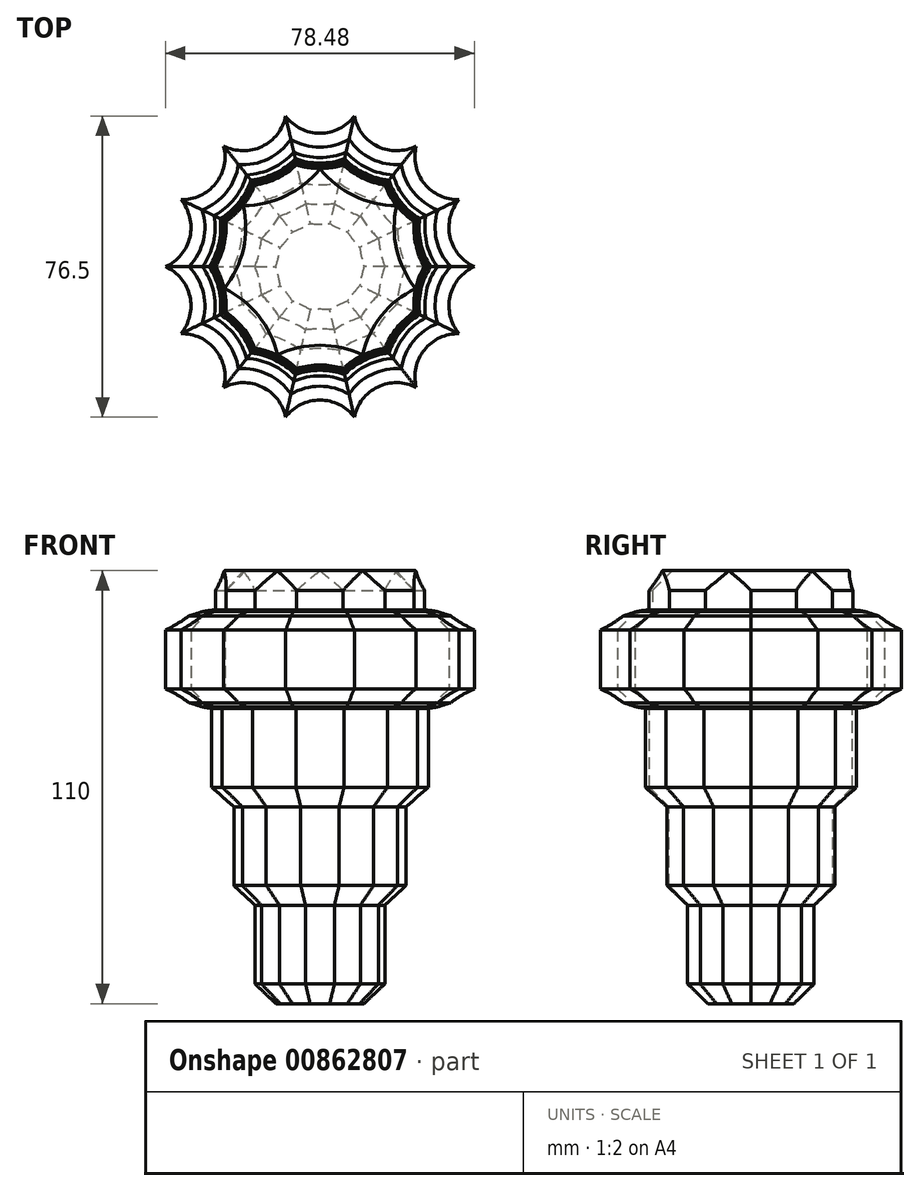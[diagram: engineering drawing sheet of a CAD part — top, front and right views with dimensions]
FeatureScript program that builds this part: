
annotation { "Feature Type Name" : "Feature", "Feature Type Description" : "" }
export const myFeature = defineFeature(function(context is Context, id is Id, definition is map)
    precondition{}
    {
        {
            var Q0;
            Q0=qCreatedBy(makeId("Top.planeOp"),FACE);
            var sketch = newSketch(context, id + "F0", { "sketchPlane" : qUnion([Q0])});
            skCircle(sketch, "E0", {"center": v(0, 44.83) * mm, "radius": 10.93 * mm});
            skCircle(sketch, "E1.1.0", {"center": v(-19.45, 40.39) * mm, "radius": 10.93 * mm});
            skCircle(sketch, "E1.2.0", {"center": v(-35.05, 27.95) * mm, "radius": 10.93 * mm});
            skCircle(sketch, "E1.3.0", {"center": v(-43.7, 9.98) * mm, "radius": 10.93 * mm});
            skCircle(sketch, "E1.4.0", {"center": v(-43.7, -9.98) * mm, "radius": 10.93 * mm});
            skCircle(sketch, "E1.5.0", {"center": v(-35.05, -27.95) * mm, "radius": 10.93 * mm});
            skCircle(sketch, "E1.6.0", {"center": v(-19.45, -40.39) * mm, "radius": 10.93 * mm});
            skCircle(sketch, "E1.7.0", {"center": v(0, -44.83) * mm, "radius": 10.93 * mm});
            skCircle(sketch, "E1.8.0", {"center": v(19.45, -40.39) * mm, "radius": 10.93 * mm});
            skCircle(sketch, "E1.9.0", {"center": v(35.05, -27.95) * mm, "radius": 10.93 * mm});
            skPoint(sketch, "E1.center", {"position": v(0, 0) * mm});
            skCircle(sketch, "E2.1.10.0", {"center": v(43.7, -9.98) * mm, "radius": 10.93 * mm});
            skCircle(sketch, "E2.1.11.0", {"center": v(43.7, 9.98) * mm, "radius": 10.93 * mm});
            skCircle(sketch, "E3.1.12.0", {"center": v(35.05, 27.95) * mm, "radius": 10.93 * mm});
            skCircle(sketch, "E3.1.13.0", {"center": v(19.45, 40.39) * mm, "radius": 10.93 * mm});
            skSolve(sketch);
        }
        {
            var Q0;
            {var subQ15=sQuery(id+"F0.wireOp",EDGE,"E1.1.0");var subQ16=sQuery(id+"F0.wireOp",EDGE,"E0");var subQ17=makeQuery(id+"F0.imprint","INTERSECT",VERTEX,{"disambiguationData":[OD(1.0)],"derivedFrom":[subQ16,subQ15]});Q0=makeQuery(id+"F0.imprint","IMPRINT",FACE,{"disambiguationData":[TD([[makeQuery(id+"F0.imprint","IMPRINT",EDGE,{"disambiguationData":[TD([[subQ17,-1.0]])],"derivedFrom":subQ16}),-1.0]])]});}
            extrude(context, id + "F1", {"entities" : qUnion([Q0]), "depth" : 25 * mm, "offsetDistance" : 25 * mm});
        }
        {
            var Q0;
            Q0=makeQuery(id+"F1.opExtrude","CAP_EDGE",EDGE,{"disambiguationData":[OSD([sQuery(id+"F0.wireOp",EDGE,"E1.2.0")])],"isStart":false});
            var Q1;
            Q1=makeQuery(id+"F1.opExtrude","CAP_EDGE",EDGE,{"disambiguationData":[OSD([sQuery(id+"F0.wireOp",EDGE,"E1.1.0")])],"isStart":false});
            var Q2;
            Q2=makeQuery(id+"F1.opExtrude","CAP_EDGE",EDGE,{"disambiguationData":[OSD([sQuery(id+"F0.wireOp",EDGE,"E0")])],"isStart":false});
            var Q3;
            Q3=makeQuery(id+"F1.opExtrude","CAP_EDGE",EDGE,{"disambiguationData":[OSD([sQuery(id+"F0.wireOp",EDGE,"E3.1.13.0")])],"isStart":false});
            var Q4;
            Q4=makeQuery(id+"F1.opExtrude","CAP_EDGE",EDGE,{"disambiguationData":[OSD([sQuery(id+"F0.wireOp",EDGE,"E3.1.12.0")])],"isStart":false});
            var Q5;
            Q5=makeQuery(id+"F1.opExtrude","CAP_EDGE",EDGE,{"disambiguationData":[OSD([sQuery(id+"F0.wireOp",EDGE,"E2.1.11.0")])],"isStart":false});
            var Q6;
            Q6=makeQuery(id+"F1.opExtrude","CAP_EDGE",EDGE,{"disambiguationData":[OSD([sQuery(id+"F0.wireOp",EDGE,"E2.1.10.0")])],"isStart":false});
            var Q7;
            Q7=makeQuery(id+"F1.opExtrude","CAP_EDGE",EDGE,{"disambiguationData":[OSD([sQuery(id+"F0.wireOp",EDGE,"E1.9.0")])],"isStart":false});
            var Q8;
            Q8=makeQuery(id+"F1.opExtrude","CAP_EDGE",EDGE,{"disambiguationData":[OSD([sQuery(id+"F0.wireOp",EDGE,"E1.8.0")])],"isStart":false});
            var Q9;
            Q9=makeQuery(id+"F1.opExtrude","CAP_EDGE",EDGE,{"disambiguationData":[OSD([sQuery(id+"F0.wireOp",EDGE,"E1.7.0")])],"isStart":false});
            var Q10;
            Q10=makeQuery(id+"F1.opExtrude","CAP_EDGE",EDGE,{"disambiguationData":[OSD([sQuery(id+"F0.wireOp",EDGE,"E1.6.0")])],"isStart":false});
            var Q11;
            Q11=makeQuery(id+"F1.opExtrude","CAP_EDGE",EDGE,{"disambiguationData":[OSD([sQuery(id+"F0.wireOp",EDGE,"E1.5.0")])],"isStart":false});
            var Q12;
            Q12=makeQuery(id+"F1.opExtrude","CAP_EDGE",EDGE,{"disambiguationData":[OSD([sQuery(id+"F0.wireOp",EDGE,"E1.4.0")])],"isStart":false});
            var Q13;
            Q13=makeQuery(id+"F1.opExtrude","CAP_EDGE",EDGE,{"disambiguationData":[OSD([sQuery(id+"F0.wireOp",EDGE,"E1.3.0")])],"isStart":false});
            chamfer(context, id + "F2", {"entities" : qUnion([Q0, Q1, Q2, Q3, Q4, Q5, Q6, Q7, Q8, Q9, Q10, Q11, Q12, Q13]), "width" : 5 * mm, "tangentPropagation" : true});
        }
        {
            var Q0;
            {var subQ0=sQuery(id+"F0.wireOp",EDGE,"E1.2.0");Q0=makeQuery(id+"F2.opChamfer","BLEND_EDGE",EDGE,{"blendedFrom":[makeQuery(id+"F1.opExtrude","CAP_EDGE",EDGE,{"disambiguationData":[OSD([subQ0])],"isStart":false}),makeQuery(id+"F1.opExtrude","CAP_FACE",FACE,{"disambiguationData":[OSD([sQuery(id+"F0.wireOp",EDGE,"E0"),sQuery(id+"F0.wireOp",EDGE,"E1.1.0"),subQ0,sQuery(id+"F0.wireOp",EDGE,"E1.3.0"),sQuery(id+"F0.wireOp",EDGE,"E1.4.0"),sQuery(id+"F0.wireOp",EDGE,"E1.5.0"),sQuery(id+"F0.wireOp",EDGE,"E1.6.0"),sQuery(id+"F0.wireOp",EDGE,"E1.7.0"),sQuery(id+"F0.wireOp",EDGE,"E1.8.0"),sQuery(id+"F0.wireOp",EDGE,"E1.9.0"),sQuery(id+"F0.wireOp",EDGE,"E2.1.10.0"),sQuery(id+"F0.wireOp",EDGE,"E2.1.11.0"),sQuery(id+"F0.wireOp",EDGE,"E3.1.12.0"),sQuery(id+"F0.wireOp",EDGE,"E3.1.13.0")])],"isStart":false})],"blendedInto":[makeQuery(id+"F1.opExtrude","CAP_FACE",FACE,{"disambiguationData":[OSD([sQuery(id+"F0.wireOp",EDGE,"E0"),sQuery(id+"F0.wireOp",EDGE,"E1.1.0"),subQ0,sQuery(id+"F0.wireOp",EDGE,"E1.3.0"),sQuery(id+"F0.wireOp",EDGE,"E1.4.0"),sQuery(id+"F0.wireOp",EDGE,"E1.5.0"),sQuery(id+"F0.wireOp",EDGE,"E1.6.0"),sQuery(id+"F0.wireOp",EDGE,"E1.7.0"),sQuery(id+"F0.wireOp",EDGE,"E1.8.0"),sQuery(id+"F0.wireOp",EDGE,"E1.9.0"),sQuery(id+"F0.wireOp",EDGE,"E2.1.10.0"),sQuery(id+"F0.wireOp",EDGE,"E2.1.11.0"),sQuery(id+"F0.wireOp",EDGE,"E3.1.12.0"),sQuery(id+"F0.wireOp",EDGE,"E3.1.13.0")])],"isStart":false})]});}
            var Q1;
            {var subQ0=sQuery(id+"F0.wireOp",EDGE,"E1.1.0");Q1=makeQuery(id+"F2.opChamfer","BLEND_EDGE",EDGE,{"blendedFrom":[makeQuery(id+"F1.opExtrude","CAP_EDGE",EDGE,{"disambiguationData":[OSD([subQ0])],"isStart":false}),makeQuery(id+"F1.opExtrude","CAP_FACE",FACE,{"disambiguationData":[OSD([sQuery(id+"F0.wireOp",EDGE,"E0"),subQ0,sQuery(id+"F0.wireOp",EDGE,"E1.2.0"),sQuery(id+"F0.wireOp",EDGE,"E1.3.0"),sQuery(id+"F0.wireOp",EDGE,"E1.4.0"),sQuery(id+"F0.wireOp",EDGE,"E1.5.0"),sQuery(id+"F0.wireOp",EDGE,"E1.6.0"),sQuery(id+"F0.wireOp",EDGE,"E1.7.0"),sQuery(id+"F0.wireOp",EDGE,"E1.8.0"),sQuery(id+"F0.wireOp",EDGE,"E1.9.0"),sQuery(id+"F0.wireOp",EDGE,"E2.1.10.0"),sQuery(id+"F0.wireOp",EDGE,"E2.1.11.0"),sQuery(id+"F0.wireOp",EDGE,"E3.1.12.0"),sQuery(id+"F0.wireOp",EDGE,"E3.1.13.0")])],"isStart":false})],"blendedInto":[makeQuery(id+"F1.opExtrude","CAP_FACE",FACE,{"disambiguationData":[OSD([sQuery(id+"F0.wireOp",EDGE,"E0"),subQ0,sQuery(id+"F0.wireOp",EDGE,"E1.2.0"),sQuery(id+"F0.wireOp",EDGE,"E1.3.0"),sQuery(id+"F0.wireOp",EDGE,"E1.4.0"),sQuery(id+"F0.wireOp",EDGE,"E1.5.0"),sQuery(id+"F0.wireOp",EDGE,"E1.6.0"),sQuery(id+"F0.wireOp",EDGE,"E1.7.0"),sQuery(id+"F0.wireOp",EDGE,"E1.8.0"),sQuery(id+"F0.wireOp",EDGE,"E1.9.0"),sQuery(id+"F0.wireOp",EDGE,"E2.1.10.0"),sQuery(id+"F0.wireOp",EDGE,"E2.1.11.0"),sQuery(id+"F0.wireOp",EDGE,"E3.1.12.0"),sQuery(id+"F0.wireOp",EDGE,"E3.1.13.0")])],"isStart":false})]});}
            var Q2;
            {var subQ0=sQuery(id+"F0.wireOp",EDGE,"E0");Q2=makeQuery(id+"F2.opChamfer","BLEND_EDGE",EDGE,{"blendedFrom":[makeQuery(id+"F1.opExtrude","CAP_EDGE",EDGE,{"disambiguationData":[OSD([subQ0])],"isStart":false}),makeQuery(id+"F1.opExtrude","CAP_FACE",FACE,{"disambiguationData":[OSD([subQ0,sQuery(id+"F0.wireOp",EDGE,"E1.1.0"),sQuery(id+"F0.wireOp",EDGE,"E1.2.0"),sQuery(id+"F0.wireOp",EDGE,"E1.3.0"),sQuery(id+"F0.wireOp",EDGE,"E1.4.0"),sQuery(id+"F0.wireOp",EDGE,"E1.5.0"),sQuery(id+"F0.wireOp",EDGE,"E1.6.0"),sQuery(id+"F0.wireOp",EDGE,"E1.7.0"),sQuery(id+"F0.wireOp",EDGE,"E1.8.0"),sQuery(id+"F0.wireOp",EDGE,"E1.9.0"),sQuery(id+"F0.wireOp",EDGE,"E2.1.10.0"),sQuery(id+"F0.wireOp",EDGE,"E2.1.11.0"),sQuery(id+"F0.wireOp",EDGE,"E3.1.12.0"),sQuery(id+"F0.wireOp",EDGE,"E3.1.13.0")])],"isStart":false})],"blendedInto":[makeQuery(id+"F1.opExtrude","CAP_FACE",FACE,{"disambiguationData":[OSD([subQ0,sQuery(id+"F0.wireOp",EDGE,"E1.1.0"),sQuery(id+"F0.wireOp",EDGE,"E1.2.0"),sQuery(id+"F0.wireOp",EDGE,"E1.3.0"),sQuery(id+"F0.wireOp",EDGE,"E1.4.0"),sQuery(id+"F0.wireOp",EDGE,"E1.5.0"),sQuery(id+"F0.wireOp",EDGE,"E1.6.0"),sQuery(id+"F0.wireOp",EDGE,"E1.7.0"),sQuery(id+"F0.wireOp",EDGE,"E1.8.0"),sQuery(id+"F0.wireOp",EDGE,"E1.9.0"),sQuery(id+"F0.wireOp",EDGE,"E2.1.10.0"),sQuery(id+"F0.wireOp",EDGE,"E2.1.11.0"),sQuery(id+"F0.wireOp",EDGE,"E3.1.12.0"),sQuery(id+"F0.wireOp",EDGE,"E3.1.13.0")])],"isStart":false})]});}
            var Q3;
            {var subQ0=sQuery(id+"F0.wireOp",EDGE,"E3.1.13.0");Q3=makeQuery(id+"F2.opChamfer","BLEND_EDGE",EDGE,{"blendedFrom":[makeQuery(id+"F1.opExtrude","CAP_EDGE",EDGE,{"disambiguationData":[OSD([subQ0])],"isStart":false}),makeQuery(id+"F1.opExtrude","CAP_FACE",FACE,{"disambiguationData":[OSD([sQuery(id+"F0.wireOp",EDGE,"E0"),sQuery(id+"F0.wireOp",EDGE,"E1.1.0"),sQuery(id+"F0.wireOp",EDGE,"E1.2.0"),sQuery(id+"F0.wireOp",EDGE,"E1.3.0"),sQuery(id+"F0.wireOp",EDGE,"E1.4.0"),sQuery(id+"F0.wireOp",EDGE,"E1.5.0"),sQuery(id+"F0.wireOp",EDGE,"E1.6.0"),sQuery(id+"F0.wireOp",EDGE,"E1.7.0"),sQuery(id+"F0.wireOp",EDGE,"E1.8.0"),sQuery(id+"F0.wireOp",EDGE,"E1.9.0"),sQuery(id+"F0.wireOp",EDGE,"E2.1.10.0"),sQuery(id+"F0.wireOp",EDGE,"E2.1.11.0"),sQuery(id+"F0.wireOp",EDGE,"E3.1.12.0"),subQ0])],"isStart":false})],"blendedInto":[makeQuery(id+"F1.opExtrude","CAP_FACE",FACE,{"disambiguationData":[OSD([sQuery(id+"F0.wireOp",EDGE,"E0"),sQuery(id+"F0.wireOp",EDGE,"E1.1.0"),sQuery(id+"F0.wireOp",EDGE,"E1.2.0"),sQuery(id+"F0.wireOp",EDGE,"E1.3.0"),sQuery(id+"F0.wireOp",EDGE,"E1.4.0"),sQuery(id+"F0.wireOp",EDGE,"E1.5.0"),sQuery(id+"F0.wireOp",EDGE,"E1.6.0"),sQuery(id+"F0.wireOp",EDGE,"E1.7.0"),sQuery(id+"F0.wireOp",EDGE,"E1.8.0"),sQuery(id+"F0.wireOp",EDGE,"E1.9.0"),sQuery(id+"F0.wireOp",EDGE,"E2.1.10.0"),sQuery(id+"F0.wireOp",EDGE,"E2.1.11.0"),sQuery(id+"F0.wireOp",EDGE,"E3.1.12.0"),subQ0])],"isStart":false})]});}
            var Q4;
            {var subQ0=sQuery(id+"F0.wireOp",EDGE,"E3.1.12.0");Q4=makeQuery(id+"F2.opChamfer","BLEND_EDGE",EDGE,{"blendedFrom":[makeQuery(id+"F1.opExtrude","CAP_EDGE",EDGE,{"disambiguationData":[OSD([subQ0])],"isStart":false}),makeQuery(id+"F1.opExtrude","CAP_FACE",FACE,{"disambiguationData":[OSD([sQuery(id+"F0.wireOp",EDGE,"E0"),sQuery(id+"F0.wireOp",EDGE,"E1.1.0"),sQuery(id+"F0.wireOp",EDGE,"E1.2.0"),sQuery(id+"F0.wireOp",EDGE,"E1.3.0"),sQuery(id+"F0.wireOp",EDGE,"E1.4.0"),sQuery(id+"F0.wireOp",EDGE,"E1.5.0"),sQuery(id+"F0.wireOp",EDGE,"E1.6.0"),sQuery(id+"F0.wireOp",EDGE,"E1.7.0"),sQuery(id+"F0.wireOp",EDGE,"E1.8.0"),sQuery(id+"F0.wireOp",EDGE,"E1.9.0"),sQuery(id+"F0.wireOp",EDGE,"E2.1.10.0"),sQuery(id+"F0.wireOp",EDGE,"E2.1.11.0"),subQ0,sQuery(id+"F0.wireOp",EDGE,"E3.1.13.0")])],"isStart":false})],"blendedInto":[makeQuery(id+"F1.opExtrude","CAP_FACE",FACE,{"disambiguationData":[OSD([sQuery(id+"F0.wireOp",EDGE,"E0"),sQuery(id+"F0.wireOp",EDGE,"E1.1.0"),sQuery(id+"F0.wireOp",EDGE,"E1.2.0"),sQuery(id+"F0.wireOp",EDGE,"E1.3.0"),sQuery(id+"F0.wireOp",EDGE,"E1.4.0"),sQuery(id+"F0.wireOp",EDGE,"E1.5.0"),sQuery(id+"F0.wireOp",EDGE,"E1.6.0"),sQuery(id+"F0.wireOp",EDGE,"E1.7.0"),sQuery(id+"F0.wireOp",EDGE,"E1.8.0"),sQuery(id+"F0.wireOp",EDGE,"E1.9.0"),sQuery(id+"F0.wireOp",EDGE,"E2.1.10.0"),sQuery(id+"F0.wireOp",EDGE,"E2.1.11.0"),subQ0,sQuery(id+"F0.wireOp",EDGE,"E3.1.13.0")])],"isStart":false})]});}
            var Q5;
            {var subQ0=sQuery(id+"F0.wireOp",EDGE,"E2.1.11.0");Q5=makeQuery(id+"F2.opChamfer","BLEND_EDGE",EDGE,{"blendedFrom":[makeQuery(id+"F1.opExtrude","CAP_EDGE",EDGE,{"disambiguationData":[OSD([subQ0])],"isStart":false}),makeQuery(id+"F1.opExtrude","CAP_FACE",FACE,{"disambiguationData":[OSD([sQuery(id+"F0.wireOp",EDGE,"E0"),sQuery(id+"F0.wireOp",EDGE,"E1.1.0"),sQuery(id+"F0.wireOp",EDGE,"E1.2.0"),sQuery(id+"F0.wireOp",EDGE,"E1.3.0"),sQuery(id+"F0.wireOp",EDGE,"E1.4.0"),sQuery(id+"F0.wireOp",EDGE,"E1.5.0"),sQuery(id+"F0.wireOp",EDGE,"E1.6.0"),sQuery(id+"F0.wireOp",EDGE,"E1.7.0"),sQuery(id+"F0.wireOp",EDGE,"E1.8.0"),sQuery(id+"F0.wireOp",EDGE,"E1.9.0"),sQuery(id+"F0.wireOp",EDGE,"E2.1.10.0"),subQ0,sQuery(id+"F0.wireOp",EDGE,"E3.1.12.0"),sQuery(id+"F0.wireOp",EDGE,"E3.1.13.0")])],"isStart":false})],"blendedInto":[makeQuery(id+"F1.opExtrude","CAP_FACE",FACE,{"disambiguationData":[OSD([sQuery(id+"F0.wireOp",EDGE,"E0"),sQuery(id+"F0.wireOp",EDGE,"E1.1.0"),sQuery(id+"F0.wireOp",EDGE,"E1.2.0"),sQuery(id+"F0.wireOp",EDGE,"E1.3.0"),sQuery(id+"F0.wireOp",EDGE,"E1.4.0"),sQuery(id+"F0.wireOp",EDGE,"E1.5.0"),sQuery(id+"F0.wireOp",EDGE,"E1.6.0"),sQuery(id+"F0.wireOp",EDGE,"E1.7.0"),sQuery(id+"F0.wireOp",EDGE,"E1.8.0"),sQuery(id+"F0.wireOp",EDGE,"E1.9.0"),sQuery(id+"F0.wireOp",EDGE,"E2.1.10.0"),subQ0,sQuery(id+"F0.wireOp",EDGE,"E3.1.12.0"),sQuery(id+"F0.wireOp",EDGE,"E3.1.13.0")])],"isStart":false})]});}
            var Q6;
            {var subQ0=sQuery(id+"F0.wireOp",EDGE,"E2.1.10.0");Q6=makeQuery(id+"F2.opChamfer","BLEND_EDGE",EDGE,{"blendedFrom":[makeQuery(id+"F1.opExtrude","CAP_EDGE",EDGE,{"disambiguationData":[OSD([subQ0])],"isStart":false}),makeQuery(id+"F1.opExtrude","CAP_FACE",FACE,{"disambiguationData":[OSD([sQuery(id+"F0.wireOp",EDGE,"E0"),sQuery(id+"F0.wireOp",EDGE,"E1.1.0"),sQuery(id+"F0.wireOp",EDGE,"E1.2.0"),sQuery(id+"F0.wireOp",EDGE,"E1.3.0"),sQuery(id+"F0.wireOp",EDGE,"E1.4.0"),sQuery(id+"F0.wireOp",EDGE,"E1.5.0"),sQuery(id+"F0.wireOp",EDGE,"E1.6.0"),sQuery(id+"F0.wireOp",EDGE,"E1.7.0"),sQuery(id+"F0.wireOp",EDGE,"E1.8.0"),sQuery(id+"F0.wireOp",EDGE,"E1.9.0"),subQ0,sQuery(id+"F0.wireOp",EDGE,"E2.1.11.0"),sQuery(id+"F0.wireOp",EDGE,"E3.1.12.0"),sQuery(id+"F0.wireOp",EDGE,"E3.1.13.0")])],"isStart":false})],"blendedInto":[makeQuery(id+"F1.opExtrude","CAP_FACE",FACE,{"disambiguationData":[OSD([sQuery(id+"F0.wireOp",EDGE,"E0"),sQuery(id+"F0.wireOp",EDGE,"E1.1.0"),sQuery(id+"F0.wireOp",EDGE,"E1.2.0"),sQuery(id+"F0.wireOp",EDGE,"E1.3.0"),sQuery(id+"F0.wireOp",EDGE,"E1.4.0"),sQuery(id+"F0.wireOp",EDGE,"E1.5.0"),sQuery(id+"F0.wireOp",EDGE,"E1.6.0"),sQuery(id+"F0.wireOp",EDGE,"E1.7.0"),sQuery(id+"F0.wireOp",EDGE,"E1.8.0"),sQuery(id+"F0.wireOp",EDGE,"E1.9.0"),subQ0,sQuery(id+"F0.wireOp",EDGE,"E2.1.11.0"),sQuery(id+"F0.wireOp",EDGE,"E3.1.12.0"),sQuery(id+"F0.wireOp",EDGE,"E3.1.13.0")])],"isStart":false})]});}
            var Q7;
            {var subQ0=sQuery(id+"F0.wireOp",EDGE,"E1.9.0");Q7=makeQuery(id+"F2.opChamfer","BLEND_EDGE",EDGE,{"blendedFrom":[makeQuery(id+"F1.opExtrude","CAP_EDGE",EDGE,{"disambiguationData":[OSD([subQ0])],"isStart":false}),makeQuery(id+"F1.opExtrude","CAP_FACE",FACE,{"disambiguationData":[OSD([sQuery(id+"F0.wireOp",EDGE,"E0"),sQuery(id+"F0.wireOp",EDGE,"E1.1.0"),sQuery(id+"F0.wireOp",EDGE,"E1.2.0"),sQuery(id+"F0.wireOp",EDGE,"E1.3.0"),sQuery(id+"F0.wireOp",EDGE,"E1.4.0"),sQuery(id+"F0.wireOp",EDGE,"E1.5.0"),sQuery(id+"F0.wireOp",EDGE,"E1.6.0"),sQuery(id+"F0.wireOp",EDGE,"E1.7.0"),sQuery(id+"F0.wireOp",EDGE,"E1.8.0"),subQ0,sQuery(id+"F0.wireOp",EDGE,"E2.1.10.0"),sQuery(id+"F0.wireOp",EDGE,"E2.1.11.0"),sQuery(id+"F0.wireOp",EDGE,"E3.1.12.0"),sQuery(id+"F0.wireOp",EDGE,"E3.1.13.0")])],"isStart":false})],"blendedInto":[makeQuery(id+"F1.opExtrude","CAP_FACE",FACE,{"disambiguationData":[OSD([sQuery(id+"F0.wireOp",EDGE,"E0"),sQuery(id+"F0.wireOp",EDGE,"E1.1.0"),sQuery(id+"F0.wireOp",EDGE,"E1.2.0"),sQuery(id+"F0.wireOp",EDGE,"E1.3.0"),sQuery(id+"F0.wireOp",EDGE,"E1.4.0"),sQuery(id+"F0.wireOp",EDGE,"E1.5.0"),sQuery(id+"F0.wireOp",EDGE,"E1.6.0"),sQuery(id+"F0.wireOp",EDGE,"E1.7.0"),sQuery(id+"F0.wireOp",EDGE,"E1.8.0"),subQ0,sQuery(id+"F0.wireOp",EDGE,"E2.1.10.0"),sQuery(id+"F0.wireOp",EDGE,"E2.1.11.0"),sQuery(id+"F0.wireOp",EDGE,"E3.1.12.0"),sQuery(id+"F0.wireOp",EDGE,"E3.1.13.0")])],"isStart":false})]});}
            var Q8;
            {var subQ0=sQuery(id+"F0.wireOp",EDGE,"E1.8.0");Q8=makeQuery(id+"F2.opChamfer","BLEND_EDGE",EDGE,{"blendedFrom":[makeQuery(id+"F1.opExtrude","CAP_EDGE",EDGE,{"disambiguationData":[OSD([subQ0])],"isStart":false}),makeQuery(id+"F1.opExtrude","CAP_FACE",FACE,{"disambiguationData":[OSD([sQuery(id+"F0.wireOp",EDGE,"E0"),sQuery(id+"F0.wireOp",EDGE,"E1.1.0"),sQuery(id+"F0.wireOp",EDGE,"E1.2.0"),sQuery(id+"F0.wireOp",EDGE,"E1.3.0"),sQuery(id+"F0.wireOp",EDGE,"E1.4.0"),sQuery(id+"F0.wireOp",EDGE,"E1.5.0"),sQuery(id+"F0.wireOp",EDGE,"E1.6.0"),sQuery(id+"F0.wireOp",EDGE,"E1.7.0"),subQ0,sQuery(id+"F0.wireOp",EDGE,"E1.9.0"),sQuery(id+"F0.wireOp",EDGE,"E2.1.10.0"),sQuery(id+"F0.wireOp",EDGE,"E2.1.11.0"),sQuery(id+"F0.wireOp",EDGE,"E3.1.12.0"),sQuery(id+"F0.wireOp",EDGE,"E3.1.13.0")])],"isStart":false})],"blendedInto":[makeQuery(id+"F1.opExtrude","CAP_FACE",FACE,{"disambiguationData":[OSD([sQuery(id+"F0.wireOp",EDGE,"E0"),sQuery(id+"F0.wireOp",EDGE,"E1.1.0"),sQuery(id+"F0.wireOp",EDGE,"E1.2.0"),sQuery(id+"F0.wireOp",EDGE,"E1.3.0"),sQuery(id+"F0.wireOp",EDGE,"E1.4.0"),sQuery(id+"F0.wireOp",EDGE,"E1.5.0"),sQuery(id+"F0.wireOp",EDGE,"E1.6.0"),sQuery(id+"F0.wireOp",EDGE,"E1.7.0"),subQ0,sQuery(id+"F0.wireOp",EDGE,"E1.9.0"),sQuery(id+"F0.wireOp",EDGE,"E2.1.10.0"),sQuery(id+"F0.wireOp",EDGE,"E2.1.11.0"),sQuery(id+"F0.wireOp",EDGE,"E3.1.12.0"),sQuery(id+"F0.wireOp",EDGE,"E3.1.13.0")])],"isStart":false})]});}
            var Q9;
            {var subQ0=sQuery(id+"F0.wireOp",EDGE,"E1.7.0");Q9=makeQuery(id+"F2.opChamfer","BLEND_EDGE",EDGE,{"blendedFrom":[makeQuery(id+"F1.opExtrude","CAP_EDGE",EDGE,{"disambiguationData":[OSD([subQ0])],"isStart":false}),makeQuery(id+"F1.opExtrude","CAP_FACE",FACE,{"disambiguationData":[OSD([sQuery(id+"F0.wireOp",EDGE,"E0"),sQuery(id+"F0.wireOp",EDGE,"E1.1.0"),sQuery(id+"F0.wireOp",EDGE,"E1.2.0"),sQuery(id+"F0.wireOp",EDGE,"E1.3.0"),sQuery(id+"F0.wireOp",EDGE,"E1.4.0"),sQuery(id+"F0.wireOp",EDGE,"E1.5.0"),sQuery(id+"F0.wireOp",EDGE,"E1.6.0"),subQ0,sQuery(id+"F0.wireOp",EDGE,"E1.8.0"),sQuery(id+"F0.wireOp",EDGE,"E1.9.0"),sQuery(id+"F0.wireOp",EDGE,"E2.1.10.0"),sQuery(id+"F0.wireOp",EDGE,"E2.1.11.0"),sQuery(id+"F0.wireOp",EDGE,"E3.1.12.0"),sQuery(id+"F0.wireOp",EDGE,"E3.1.13.0")])],"isStart":false})],"blendedInto":[makeQuery(id+"F1.opExtrude","CAP_FACE",FACE,{"disambiguationData":[OSD([sQuery(id+"F0.wireOp",EDGE,"E0"),sQuery(id+"F0.wireOp",EDGE,"E1.1.0"),sQuery(id+"F0.wireOp",EDGE,"E1.2.0"),sQuery(id+"F0.wireOp",EDGE,"E1.3.0"),sQuery(id+"F0.wireOp",EDGE,"E1.4.0"),sQuery(id+"F0.wireOp",EDGE,"E1.5.0"),sQuery(id+"F0.wireOp",EDGE,"E1.6.0"),subQ0,sQuery(id+"F0.wireOp",EDGE,"E1.8.0"),sQuery(id+"F0.wireOp",EDGE,"E1.9.0"),sQuery(id+"F0.wireOp",EDGE,"E2.1.10.0"),sQuery(id+"F0.wireOp",EDGE,"E2.1.11.0"),sQuery(id+"F0.wireOp",EDGE,"E3.1.12.0"),sQuery(id+"F0.wireOp",EDGE,"E3.1.13.0")])],"isStart":false})]});}
            var Q10;
            {var subQ0=sQuery(id+"F0.wireOp",EDGE,"E1.6.0");Q10=makeQuery(id+"F2.opChamfer","BLEND_EDGE",EDGE,{"blendedFrom":[makeQuery(id+"F1.opExtrude","CAP_EDGE",EDGE,{"disambiguationData":[OSD([subQ0])],"isStart":false}),makeQuery(id+"F1.opExtrude","CAP_FACE",FACE,{"disambiguationData":[OSD([sQuery(id+"F0.wireOp",EDGE,"E0"),sQuery(id+"F0.wireOp",EDGE,"E1.1.0"),sQuery(id+"F0.wireOp",EDGE,"E1.2.0"),sQuery(id+"F0.wireOp",EDGE,"E1.3.0"),sQuery(id+"F0.wireOp",EDGE,"E1.4.0"),sQuery(id+"F0.wireOp",EDGE,"E1.5.0"),subQ0,sQuery(id+"F0.wireOp",EDGE,"E1.7.0"),sQuery(id+"F0.wireOp",EDGE,"E1.8.0"),sQuery(id+"F0.wireOp",EDGE,"E1.9.0"),sQuery(id+"F0.wireOp",EDGE,"E2.1.10.0"),sQuery(id+"F0.wireOp",EDGE,"E2.1.11.0"),sQuery(id+"F0.wireOp",EDGE,"E3.1.12.0"),sQuery(id+"F0.wireOp",EDGE,"E3.1.13.0")])],"isStart":false})],"blendedInto":[makeQuery(id+"F1.opExtrude","CAP_FACE",FACE,{"disambiguationData":[OSD([sQuery(id+"F0.wireOp",EDGE,"E0"),sQuery(id+"F0.wireOp",EDGE,"E1.1.0"),sQuery(id+"F0.wireOp",EDGE,"E1.2.0"),sQuery(id+"F0.wireOp",EDGE,"E1.3.0"),sQuery(id+"F0.wireOp",EDGE,"E1.4.0"),sQuery(id+"F0.wireOp",EDGE,"E1.5.0"),subQ0,sQuery(id+"F0.wireOp",EDGE,"E1.7.0"),sQuery(id+"F0.wireOp",EDGE,"E1.8.0"),sQuery(id+"F0.wireOp",EDGE,"E1.9.0"),sQuery(id+"F0.wireOp",EDGE,"E2.1.10.0"),sQuery(id+"F0.wireOp",EDGE,"E2.1.11.0"),sQuery(id+"F0.wireOp",EDGE,"E3.1.12.0"),sQuery(id+"F0.wireOp",EDGE,"E3.1.13.0")])],"isStart":false})]});}
            var Q11;
            {var subQ0=sQuery(id+"F0.wireOp",EDGE,"E1.5.0");Q11=makeQuery(id+"F2.opChamfer","BLEND_EDGE",EDGE,{"blendedFrom":[makeQuery(id+"F1.opExtrude","CAP_EDGE",EDGE,{"disambiguationData":[OSD([subQ0])],"isStart":false}),makeQuery(id+"F1.opExtrude","CAP_FACE",FACE,{"disambiguationData":[OSD([sQuery(id+"F0.wireOp",EDGE,"E0"),sQuery(id+"F0.wireOp",EDGE,"E1.1.0"),sQuery(id+"F0.wireOp",EDGE,"E1.2.0"),sQuery(id+"F0.wireOp",EDGE,"E1.3.0"),sQuery(id+"F0.wireOp",EDGE,"E1.4.0"),subQ0,sQuery(id+"F0.wireOp",EDGE,"E1.6.0"),sQuery(id+"F0.wireOp",EDGE,"E1.7.0"),sQuery(id+"F0.wireOp",EDGE,"E1.8.0"),sQuery(id+"F0.wireOp",EDGE,"E1.9.0"),sQuery(id+"F0.wireOp",EDGE,"E2.1.10.0"),sQuery(id+"F0.wireOp",EDGE,"E2.1.11.0"),sQuery(id+"F0.wireOp",EDGE,"E3.1.12.0"),sQuery(id+"F0.wireOp",EDGE,"E3.1.13.0")])],"isStart":false})],"blendedInto":[makeQuery(id+"F1.opExtrude","CAP_FACE",FACE,{"disambiguationData":[OSD([sQuery(id+"F0.wireOp",EDGE,"E0"),sQuery(id+"F0.wireOp",EDGE,"E1.1.0"),sQuery(id+"F0.wireOp",EDGE,"E1.2.0"),sQuery(id+"F0.wireOp",EDGE,"E1.3.0"),sQuery(id+"F0.wireOp",EDGE,"E1.4.0"),subQ0,sQuery(id+"F0.wireOp",EDGE,"E1.6.0"),sQuery(id+"F0.wireOp",EDGE,"E1.7.0"),sQuery(id+"F0.wireOp",EDGE,"E1.8.0"),sQuery(id+"F0.wireOp",EDGE,"E1.9.0"),sQuery(id+"F0.wireOp",EDGE,"E2.1.10.0"),sQuery(id+"F0.wireOp",EDGE,"E2.1.11.0"),sQuery(id+"F0.wireOp",EDGE,"E3.1.12.0"),sQuery(id+"F0.wireOp",EDGE,"E3.1.13.0")])],"isStart":false})]});}
            var Q12;
            {var subQ0=sQuery(id+"F0.wireOp",EDGE,"E1.4.0");Q12=makeQuery(id+"F2.opChamfer","BLEND_EDGE",EDGE,{"blendedFrom":[makeQuery(id+"F1.opExtrude","CAP_EDGE",EDGE,{"disambiguationData":[OSD([subQ0])],"isStart":false}),makeQuery(id+"F1.opExtrude","CAP_FACE",FACE,{"disambiguationData":[OSD([sQuery(id+"F0.wireOp",EDGE,"E0"),sQuery(id+"F0.wireOp",EDGE,"E1.1.0"),sQuery(id+"F0.wireOp",EDGE,"E1.2.0"),sQuery(id+"F0.wireOp",EDGE,"E1.3.0"),subQ0,sQuery(id+"F0.wireOp",EDGE,"E1.5.0"),sQuery(id+"F0.wireOp",EDGE,"E1.6.0"),sQuery(id+"F0.wireOp",EDGE,"E1.7.0"),sQuery(id+"F0.wireOp",EDGE,"E1.8.0"),sQuery(id+"F0.wireOp",EDGE,"E1.9.0"),sQuery(id+"F0.wireOp",EDGE,"E2.1.10.0"),sQuery(id+"F0.wireOp",EDGE,"E2.1.11.0"),sQuery(id+"F0.wireOp",EDGE,"E3.1.12.0"),sQuery(id+"F0.wireOp",EDGE,"E3.1.13.0")])],"isStart":false})],"blendedInto":[makeQuery(id+"F1.opExtrude","CAP_FACE",FACE,{"disambiguationData":[OSD([sQuery(id+"F0.wireOp",EDGE,"E0"),sQuery(id+"F0.wireOp",EDGE,"E1.1.0"),sQuery(id+"F0.wireOp",EDGE,"E1.2.0"),sQuery(id+"F0.wireOp",EDGE,"E1.3.0"),subQ0,sQuery(id+"F0.wireOp",EDGE,"E1.5.0"),sQuery(id+"F0.wireOp",EDGE,"E1.6.0"),sQuery(id+"F0.wireOp",EDGE,"E1.7.0"),sQuery(id+"F0.wireOp",EDGE,"E1.8.0"),sQuery(id+"F0.wireOp",EDGE,"E1.9.0"),sQuery(id+"F0.wireOp",EDGE,"E2.1.10.0"),sQuery(id+"F0.wireOp",EDGE,"E2.1.11.0"),sQuery(id+"F0.wireOp",EDGE,"E3.1.12.0"),sQuery(id+"F0.wireOp",EDGE,"E3.1.13.0")])],"isStart":false})]});}
            var Q13;
            {var subQ0=sQuery(id+"F0.wireOp",EDGE,"E1.3.0");Q13=makeQuery(id+"F2.opChamfer","BLEND_EDGE",EDGE,{"blendedFrom":[makeQuery(id+"F1.opExtrude","CAP_EDGE",EDGE,{"disambiguationData":[OSD([subQ0])],"isStart":false}),makeQuery(id+"F1.opExtrude","CAP_FACE",FACE,{"disambiguationData":[OSD([sQuery(id+"F0.wireOp",EDGE,"E0"),sQuery(id+"F0.wireOp",EDGE,"E1.1.0"),sQuery(id+"F0.wireOp",EDGE,"E1.2.0"),subQ0,sQuery(id+"F0.wireOp",EDGE,"E1.4.0"),sQuery(id+"F0.wireOp",EDGE,"E1.5.0"),sQuery(id+"F0.wireOp",EDGE,"E1.6.0"),sQuery(id+"F0.wireOp",EDGE,"E1.7.0"),sQuery(id+"F0.wireOp",EDGE,"E1.8.0"),sQuery(id+"F0.wireOp",EDGE,"E1.9.0"),sQuery(id+"F0.wireOp",EDGE,"E2.1.10.0"),sQuery(id+"F0.wireOp",EDGE,"E2.1.11.0"),sQuery(id+"F0.wireOp",EDGE,"E3.1.12.0"),sQuery(id+"F0.wireOp",EDGE,"E3.1.13.0")])],"isStart":false})],"blendedInto":[makeQuery(id+"F1.opExtrude","CAP_FACE",FACE,{"disambiguationData":[OSD([sQuery(id+"F0.wireOp",EDGE,"E0"),sQuery(id+"F0.wireOp",EDGE,"E1.1.0"),sQuery(id+"F0.wireOp",EDGE,"E1.2.0"),subQ0,sQuery(id+"F0.wireOp",EDGE,"E1.4.0"),sQuery(id+"F0.wireOp",EDGE,"E1.5.0"),sQuery(id+"F0.wireOp",EDGE,"E1.6.0"),sQuery(id+"F0.wireOp",EDGE,"E1.7.0"),sQuery(id+"F0.wireOp",EDGE,"E1.8.0"),sQuery(id+"F0.wireOp",EDGE,"E1.9.0"),sQuery(id+"F0.wireOp",EDGE,"E2.1.10.0"),sQuery(id+"F0.wireOp",EDGE,"E2.1.11.0"),sQuery(id+"F0.wireOp",EDGE,"E3.1.12.0"),sQuery(id+"F0.wireOp",EDGE,"E3.1.13.0")])],"isStart":false})]});}
            chamfer(context, id + "F3", {"entities" : qUnion([Q0, Q1, Q2, Q3, Q4, Q5, Q6, Q7, Q8, Q9, Q10, Q11, Q12, Q13]), "width" : 5 * mm, "tangentPropagation" : true});
        }
        {
            var Q0;
            {var subQ0=sQuery(id+"F0.wireOp",EDGE,"E1.2.0");var subQ1=makeQuery(id+"F1.opExtrude","CAP_FACE",FACE,{"disambiguationData":[OSD([sQuery(id+"F0.wireOp",EDGE,"E0"),sQuery(id+"F0.wireOp",EDGE,"E1.1.0"),subQ0,sQuery(id+"F0.wireOp",EDGE,"E1.3.0"),sQuery(id+"F0.wireOp",EDGE,"E1.4.0"),sQuery(id+"F0.wireOp",EDGE,"E1.5.0"),sQuery(id+"F0.wireOp",EDGE,"E1.6.0"),sQuery(id+"F0.wireOp",EDGE,"E1.7.0"),sQuery(id+"F0.wireOp",EDGE,"E1.8.0"),sQuery(id+"F0.wireOp",EDGE,"E1.9.0"),sQuery(id+"F0.wireOp",EDGE,"E2.1.10.0"),sQuery(id+"F0.wireOp",EDGE,"E2.1.11.0"),sQuery(id+"F0.wireOp",EDGE,"E3.1.12.0"),sQuery(id+"F0.wireOp",EDGE,"E3.1.13.0")])],"isStart":false});Q0=makeQuery(id+"F3.opChamfer","BLEND_EDGE",EDGE,{"blendedFrom":[makeQuery(id+"F2.opChamfer","BLEND_EDGE",EDGE,{"blendedFrom":[makeQuery(id+"F1.opExtrude","CAP_EDGE",EDGE,{"disambiguationData":[OSD([subQ0])],"isStart":false}),subQ1],"blendedInto":[subQ1]}),subQ1],"blendedInto":[subQ1]});}
            var Q1;
            {var subQ0=sQuery(id+"F0.wireOp",EDGE,"E1.1.0");var subQ1=makeQuery(id+"F1.opExtrude","CAP_FACE",FACE,{"disambiguationData":[OSD([sQuery(id+"F0.wireOp",EDGE,"E0"),subQ0,sQuery(id+"F0.wireOp",EDGE,"E1.2.0"),sQuery(id+"F0.wireOp",EDGE,"E1.3.0"),sQuery(id+"F0.wireOp",EDGE,"E1.4.0"),sQuery(id+"F0.wireOp",EDGE,"E1.5.0"),sQuery(id+"F0.wireOp",EDGE,"E1.6.0"),sQuery(id+"F0.wireOp",EDGE,"E1.7.0"),sQuery(id+"F0.wireOp",EDGE,"E1.8.0"),sQuery(id+"F0.wireOp",EDGE,"E1.9.0"),sQuery(id+"F0.wireOp",EDGE,"E2.1.10.0"),sQuery(id+"F0.wireOp",EDGE,"E2.1.11.0"),sQuery(id+"F0.wireOp",EDGE,"E3.1.12.0"),sQuery(id+"F0.wireOp",EDGE,"E3.1.13.0")])],"isStart":false});Q1=makeQuery(id+"F3.opChamfer","BLEND_EDGE",EDGE,{"blendedFrom":[makeQuery(id+"F2.opChamfer","BLEND_EDGE",EDGE,{"blendedFrom":[makeQuery(id+"F1.opExtrude","CAP_EDGE",EDGE,{"disambiguationData":[OSD([subQ0])],"isStart":false}),subQ1],"blendedInto":[subQ1]}),subQ1],"blendedInto":[subQ1]});}
            var Q2;
            {var subQ0=sQuery(id+"F0.wireOp",EDGE,"E0");var subQ1=makeQuery(id+"F1.opExtrude","CAP_FACE",FACE,{"disambiguationData":[OSD([subQ0,sQuery(id+"F0.wireOp",EDGE,"E1.1.0"),sQuery(id+"F0.wireOp",EDGE,"E1.2.0"),sQuery(id+"F0.wireOp",EDGE,"E1.3.0"),sQuery(id+"F0.wireOp",EDGE,"E1.4.0"),sQuery(id+"F0.wireOp",EDGE,"E1.5.0"),sQuery(id+"F0.wireOp",EDGE,"E1.6.0"),sQuery(id+"F0.wireOp",EDGE,"E1.7.0"),sQuery(id+"F0.wireOp",EDGE,"E1.8.0"),sQuery(id+"F0.wireOp",EDGE,"E1.9.0"),sQuery(id+"F0.wireOp",EDGE,"E2.1.10.0"),sQuery(id+"F0.wireOp",EDGE,"E2.1.11.0"),sQuery(id+"F0.wireOp",EDGE,"E3.1.12.0"),sQuery(id+"F0.wireOp",EDGE,"E3.1.13.0")])],"isStart":false});Q2=makeQuery(id+"F3.opChamfer","BLEND_EDGE",EDGE,{"blendedFrom":[makeQuery(id+"F2.opChamfer","BLEND_EDGE",EDGE,{"blendedFrom":[makeQuery(id+"F1.opExtrude","CAP_EDGE",EDGE,{"disambiguationData":[OSD([subQ0])],"isStart":false}),subQ1],"blendedInto":[subQ1]}),subQ1],"blendedInto":[subQ1]});}
            var Q3;
            {var subQ0=sQuery(id+"F0.wireOp",EDGE,"E3.1.13.0");var subQ1=makeQuery(id+"F1.opExtrude","CAP_FACE",FACE,{"disambiguationData":[OSD([sQuery(id+"F0.wireOp",EDGE,"E0"),sQuery(id+"F0.wireOp",EDGE,"E1.1.0"),sQuery(id+"F0.wireOp",EDGE,"E1.2.0"),sQuery(id+"F0.wireOp",EDGE,"E1.3.0"),sQuery(id+"F0.wireOp",EDGE,"E1.4.0"),sQuery(id+"F0.wireOp",EDGE,"E1.5.0"),sQuery(id+"F0.wireOp",EDGE,"E1.6.0"),sQuery(id+"F0.wireOp",EDGE,"E1.7.0"),sQuery(id+"F0.wireOp",EDGE,"E1.8.0"),sQuery(id+"F0.wireOp",EDGE,"E1.9.0"),sQuery(id+"F0.wireOp",EDGE,"E2.1.10.0"),sQuery(id+"F0.wireOp",EDGE,"E2.1.11.0"),sQuery(id+"F0.wireOp",EDGE,"E3.1.12.0"),subQ0])],"isStart":false});Q3=makeQuery(id+"F3.opChamfer","BLEND_EDGE",EDGE,{"blendedFrom":[makeQuery(id+"F2.opChamfer","BLEND_EDGE",EDGE,{"blendedFrom":[makeQuery(id+"F1.opExtrude","CAP_EDGE",EDGE,{"disambiguationData":[OSD([subQ0])],"isStart":false}),subQ1],"blendedInto":[subQ1]}),subQ1],"blendedInto":[subQ1]});}
            var Q4;
            {var subQ0=sQuery(id+"F0.wireOp",EDGE,"E3.1.12.0");var subQ1=makeQuery(id+"F1.opExtrude","CAP_FACE",FACE,{"disambiguationData":[OSD([sQuery(id+"F0.wireOp",EDGE,"E0"),sQuery(id+"F0.wireOp",EDGE,"E1.1.0"),sQuery(id+"F0.wireOp",EDGE,"E1.2.0"),sQuery(id+"F0.wireOp",EDGE,"E1.3.0"),sQuery(id+"F0.wireOp",EDGE,"E1.4.0"),sQuery(id+"F0.wireOp",EDGE,"E1.5.0"),sQuery(id+"F0.wireOp",EDGE,"E1.6.0"),sQuery(id+"F0.wireOp",EDGE,"E1.7.0"),sQuery(id+"F0.wireOp",EDGE,"E1.8.0"),sQuery(id+"F0.wireOp",EDGE,"E1.9.0"),sQuery(id+"F0.wireOp",EDGE,"E2.1.10.0"),sQuery(id+"F0.wireOp",EDGE,"E2.1.11.0"),subQ0,sQuery(id+"F0.wireOp",EDGE,"E3.1.13.0")])],"isStart":false});Q4=makeQuery(id+"F3.opChamfer","BLEND_EDGE",EDGE,{"blendedFrom":[makeQuery(id+"F2.opChamfer","BLEND_EDGE",EDGE,{"blendedFrom":[makeQuery(id+"F1.opExtrude","CAP_EDGE",EDGE,{"disambiguationData":[OSD([subQ0])],"isStart":false}),subQ1],"blendedInto":[subQ1]}),subQ1],"blendedInto":[subQ1]});}
            var Q5;
            {var subQ0=sQuery(id+"F0.wireOp",EDGE,"E2.1.11.0");var subQ1=makeQuery(id+"F1.opExtrude","CAP_FACE",FACE,{"disambiguationData":[OSD([sQuery(id+"F0.wireOp",EDGE,"E0"),sQuery(id+"F0.wireOp",EDGE,"E1.1.0"),sQuery(id+"F0.wireOp",EDGE,"E1.2.0"),sQuery(id+"F0.wireOp",EDGE,"E1.3.0"),sQuery(id+"F0.wireOp",EDGE,"E1.4.0"),sQuery(id+"F0.wireOp",EDGE,"E1.5.0"),sQuery(id+"F0.wireOp",EDGE,"E1.6.0"),sQuery(id+"F0.wireOp",EDGE,"E1.7.0"),sQuery(id+"F0.wireOp",EDGE,"E1.8.0"),sQuery(id+"F0.wireOp",EDGE,"E1.9.0"),sQuery(id+"F0.wireOp",EDGE,"E2.1.10.0"),subQ0,sQuery(id+"F0.wireOp",EDGE,"E3.1.12.0"),sQuery(id+"F0.wireOp",EDGE,"E3.1.13.0")])],"isStart":false});Q5=makeQuery(id+"F3.opChamfer","BLEND_EDGE",EDGE,{"blendedFrom":[makeQuery(id+"F2.opChamfer","BLEND_EDGE",EDGE,{"blendedFrom":[makeQuery(id+"F1.opExtrude","CAP_EDGE",EDGE,{"disambiguationData":[OSD([subQ0])],"isStart":false}),subQ1],"blendedInto":[subQ1]}),subQ1],"blendedInto":[subQ1]});}
            var Q6;
            {var subQ0=sQuery(id+"F0.wireOp",EDGE,"E2.1.10.0");var subQ1=makeQuery(id+"F1.opExtrude","CAP_FACE",FACE,{"disambiguationData":[OSD([sQuery(id+"F0.wireOp",EDGE,"E0"),sQuery(id+"F0.wireOp",EDGE,"E1.1.0"),sQuery(id+"F0.wireOp",EDGE,"E1.2.0"),sQuery(id+"F0.wireOp",EDGE,"E1.3.0"),sQuery(id+"F0.wireOp",EDGE,"E1.4.0"),sQuery(id+"F0.wireOp",EDGE,"E1.5.0"),sQuery(id+"F0.wireOp",EDGE,"E1.6.0"),sQuery(id+"F0.wireOp",EDGE,"E1.7.0"),sQuery(id+"F0.wireOp",EDGE,"E1.8.0"),sQuery(id+"F0.wireOp",EDGE,"E1.9.0"),subQ0,sQuery(id+"F0.wireOp",EDGE,"E2.1.11.0"),sQuery(id+"F0.wireOp",EDGE,"E3.1.12.0"),sQuery(id+"F0.wireOp",EDGE,"E3.1.13.0")])],"isStart":false});Q6=makeQuery(id+"F3.opChamfer","BLEND_EDGE",EDGE,{"blendedFrom":[makeQuery(id+"F2.opChamfer","BLEND_EDGE",EDGE,{"blendedFrom":[makeQuery(id+"F1.opExtrude","CAP_EDGE",EDGE,{"disambiguationData":[OSD([subQ0])],"isStart":false}),subQ1],"blendedInto":[subQ1]}),subQ1],"blendedInto":[subQ1]});}
            var Q7;
            {var subQ0=sQuery(id+"F0.wireOp",EDGE,"E1.9.0");var subQ1=makeQuery(id+"F1.opExtrude","CAP_FACE",FACE,{"disambiguationData":[OSD([sQuery(id+"F0.wireOp",EDGE,"E0"),sQuery(id+"F0.wireOp",EDGE,"E1.1.0"),sQuery(id+"F0.wireOp",EDGE,"E1.2.0"),sQuery(id+"F0.wireOp",EDGE,"E1.3.0"),sQuery(id+"F0.wireOp",EDGE,"E1.4.0"),sQuery(id+"F0.wireOp",EDGE,"E1.5.0"),sQuery(id+"F0.wireOp",EDGE,"E1.6.0"),sQuery(id+"F0.wireOp",EDGE,"E1.7.0"),sQuery(id+"F0.wireOp",EDGE,"E1.8.0"),subQ0,sQuery(id+"F0.wireOp",EDGE,"E2.1.10.0"),sQuery(id+"F0.wireOp",EDGE,"E2.1.11.0"),sQuery(id+"F0.wireOp",EDGE,"E3.1.12.0"),sQuery(id+"F0.wireOp",EDGE,"E3.1.13.0")])],"isStart":false});Q7=makeQuery(id+"F3.opChamfer","BLEND_EDGE",EDGE,{"blendedFrom":[makeQuery(id+"F2.opChamfer","BLEND_EDGE",EDGE,{"blendedFrom":[makeQuery(id+"F1.opExtrude","CAP_EDGE",EDGE,{"disambiguationData":[OSD([subQ0])],"isStart":false}),subQ1],"blendedInto":[subQ1]}),subQ1],"blendedInto":[subQ1]});}
            var Q8;
            {var subQ0=sQuery(id+"F0.wireOp",EDGE,"E1.8.0");var subQ1=makeQuery(id+"F1.opExtrude","CAP_FACE",FACE,{"disambiguationData":[OSD([sQuery(id+"F0.wireOp",EDGE,"E0"),sQuery(id+"F0.wireOp",EDGE,"E1.1.0"),sQuery(id+"F0.wireOp",EDGE,"E1.2.0"),sQuery(id+"F0.wireOp",EDGE,"E1.3.0"),sQuery(id+"F0.wireOp",EDGE,"E1.4.0"),sQuery(id+"F0.wireOp",EDGE,"E1.5.0"),sQuery(id+"F0.wireOp",EDGE,"E1.6.0"),sQuery(id+"F0.wireOp",EDGE,"E1.7.0"),subQ0,sQuery(id+"F0.wireOp",EDGE,"E1.9.0"),sQuery(id+"F0.wireOp",EDGE,"E2.1.10.0"),sQuery(id+"F0.wireOp",EDGE,"E2.1.11.0"),sQuery(id+"F0.wireOp",EDGE,"E3.1.12.0"),sQuery(id+"F0.wireOp",EDGE,"E3.1.13.0")])],"isStart":false});Q8=makeQuery(id+"F3.opChamfer","BLEND_EDGE",EDGE,{"blendedFrom":[makeQuery(id+"F2.opChamfer","BLEND_EDGE",EDGE,{"blendedFrom":[makeQuery(id+"F1.opExtrude","CAP_EDGE",EDGE,{"disambiguationData":[OSD([subQ0])],"isStart":false}),subQ1],"blendedInto":[subQ1]}),subQ1],"blendedInto":[subQ1]});}
            var Q9;
            {var subQ0=sQuery(id+"F0.wireOp",EDGE,"E1.7.0");var subQ1=makeQuery(id+"F1.opExtrude","CAP_FACE",FACE,{"disambiguationData":[OSD([sQuery(id+"F0.wireOp",EDGE,"E0"),sQuery(id+"F0.wireOp",EDGE,"E1.1.0"),sQuery(id+"F0.wireOp",EDGE,"E1.2.0"),sQuery(id+"F0.wireOp",EDGE,"E1.3.0"),sQuery(id+"F0.wireOp",EDGE,"E1.4.0"),sQuery(id+"F0.wireOp",EDGE,"E1.5.0"),sQuery(id+"F0.wireOp",EDGE,"E1.6.0"),subQ0,sQuery(id+"F0.wireOp",EDGE,"E1.8.0"),sQuery(id+"F0.wireOp",EDGE,"E1.9.0"),sQuery(id+"F0.wireOp",EDGE,"E2.1.10.0"),sQuery(id+"F0.wireOp",EDGE,"E2.1.11.0"),sQuery(id+"F0.wireOp",EDGE,"E3.1.12.0"),sQuery(id+"F0.wireOp",EDGE,"E3.1.13.0")])],"isStart":false});Q9=makeQuery(id+"F3.opChamfer","BLEND_EDGE",EDGE,{"blendedFrom":[makeQuery(id+"F2.opChamfer","BLEND_EDGE",EDGE,{"blendedFrom":[makeQuery(id+"F1.opExtrude","CAP_EDGE",EDGE,{"disambiguationData":[OSD([subQ0])],"isStart":false}),subQ1],"blendedInto":[subQ1]}),subQ1],"blendedInto":[subQ1]});}
            var Q10;
            {var subQ0=sQuery(id+"F0.wireOp",EDGE,"E1.6.0");var subQ1=makeQuery(id+"F1.opExtrude","CAP_FACE",FACE,{"disambiguationData":[OSD([sQuery(id+"F0.wireOp",EDGE,"E0"),sQuery(id+"F0.wireOp",EDGE,"E1.1.0"),sQuery(id+"F0.wireOp",EDGE,"E1.2.0"),sQuery(id+"F0.wireOp",EDGE,"E1.3.0"),sQuery(id+"F0.wireOp",EDGE,"E1.4.0"),sQuery(id+"F0.wireOp",EDGE,"E1.5.0"),subQ0,sQuery(id+"F0.wireOp",EDGE,"E1.7.0"),sQuery(id+"F0.wireOp",EDGE,"E1.8.0"),sQuery(id+"F0.wireOp",EDGE,"E1.9.0"),sQuery(id+"F0.wireOp",EDGE,"E2.1.10.0"),sQuery(id+"F0.wireOp",EDGE,"E2.1.11.0"),sQuery(id+"F0.wireOp",EDGE,"E3.1.12.0"),sQuery(id+"F0.wireOp",EDGE,"E3.1.13.0")])],"isStart":false});Q10=makeQuery(id+"F3.opChamfer","BLEND_EDGE",EDGE,{"blendedFrom":[makeQuery(id+"F2.opChamfer","BLEND_EDGE",EDGE,{"blendedFrom":[makeQuery(id+"F1.opExtrude","CAP_EDGE",EDGE,{"disambiguationData":[OSD([subQ0])],"isStart":false}),subQ1],"blendedInto":[subQ1]}),subQ1],"blendedInto":[subQ1]});}
            var Q11;
            {var subQ0=sQuery(id+"F0.wireOp",EDGE,"E1.5.0");var subQ1=makeQuery(id+"F1.opExtrude","CAP_FACE",FACE,{"disambiguationData":[OSD([sQuery(id+"F0.wireOp",EDGE,"E0"),sQuery(id+"F0.wireOp",EDGE,"E1.1.0"),sQuery(id+"F0.wireOp",EDGE,"E1.2.0"),sQuery(id+"F0.wireOp",EDGE,"E1.3.0"),sQuery(id+"F0.wireOp",EDGE,"E1.4.0"),subQ0,sQuery(id+"F0.wireOp",EDGE,"E1.6.0"),sQuery(id+"F0.wireOp",EDGE,"E1.7.0"),sQuery(id+"F0.wireOp",EDGE,"E1.8.0"),sQuery(id+"F0.wireOp",EDGE,"E1.9.0"),sQuery(id+"F0.wireOp",EDGE,"E2.1.10.0"),sQuery(id+"F0.wireOp",EDGE,"E2.1.11.0"),sQuery(id+"F0.wireOp",EDGE,"E3.1.12.0"),sQuery(id+"F0.wireOp",EDGE,"E3.1.13.0")])],"isStart":false});Q11=makeQuery(id+"F3.opChamfer","BLEND_EDGE",EDGE,{"blendedFrom":[makeQuery(id+"F2.opChamfer","BLEND_EDGE",EDGE,{"blendedFrom":[makeQuery(id+"F1.opExtrude","CAP_EDGE",EDGE,{"disambiguationData":[OSD([subQ0])],"isStart":false}),subQ1],"blendedInto":[subQ1]}),subQ1],"blendedInto":[subQ1]});}
            var Q12;
            {var subQ0=sQuery(id+"F0.wireOp",EDGE,"E1.4.0");var subQ1=makeQuery(id+"F1.opExtrude","CAP_FACE",FACE,{"disambiguationData":[OSD([sQuery(id+"F0.wireOp",EDGE,"E0"),sQuery(id+"F0.wireOp",EDGE,"E1.1.0"),sQuery(id+"F0.wireOp",EDGE,"E1.2.0"),sQuery(id+"F0.wireOp",EDGE,"E1.3.0"),subQ0,sQuery(id+"F0.wireOp",EDGE,"E1.5.0"),sQuery(id+"F0.wireOp",EDGE,"E1.6.0"),sQuery(id+"F0.wireOp",EDGE,"E1.7.0"),sQuery(id+"F0.wireOp",EDGE,"E1.8.0"),sQuery(id+"F0.wireOp",EDGE,"E1.9.0"),sQuery(id+"F0.wireOp",EDGE,"E2.1.10.0"),sQuery(id+"F0.wireOp",EDGE,"E2.1.11.0"),sQuery(id+"F0.wireOp",EDGE,"E3.1.12.0"),sQuery(id+"F0.wireOp",EDGE,"E3.1.13.0")])],"isStart":false});Q12=makeQuery(id+"F3.opChamfer","BLEND_EDGE",EDGE,{"blendedFrom":[makeQuery(id+"F2.opChamfer","BLEND_EDGE",EDGE,{"blendedFrom":[makeQuery(id+"F1.opExtrude","CAP_EDGE",EDGE,{"disambiguationData":[OSD([subQ0])],"isStart":false}),subQ1],"blendedInto":[subQ1]}),subQ1],"blendedInto":[subQ1]});}
            var Q13;
            {var subQ0=sQuery(id+"F0.wireOp",EDGE,"E1.3.0");var subQ1=makeQuery(id+"F1.opExtrude","CAP_FACE",FACE,{"disambiguationData":[OSD([sQuery(id+"F0.wireOp",EDGE,"E0"),sQuery(id+"F0.wireOp",EDGE,"E1.1.0"),sQuery(id+"F0.wireOp",EDGE,"E1.2.0"),subQ0,sQuery(id+"F0.wireOp",EDGE,"E1.4.0"),sQuery(id+"F0.wireOp",EDGE,"E1.5.0"),sQuery(id+"F0.wireOp",EDGE,"E1.6.0"),sQuery(id+"F0.wireOp",EDGE,"E1.7.0"),sQuery(id+"F0.wireOp",EDGE,"E1.8.0"),sQuery(id+"F0.wireOp",EDGE,"E1.9.0"),sQuery(id+"F0.wireOp",EDGE,"E2.1.10.0"),sQuery(id+"F0.wireOp",EDGE,"E2.1.11.0"),sQuery(id+"F0.wireOp",EDGE,"E3.1.12.0"),sQuery(id+"F0.wireOp",EDGE,"E3.1.13.0")])],"isStart":false});Q13=makeQuery(id+"F3.opChamfer","BLEND_EDGE",EDGE,{"blendedFrom":[makeQuery(id+"F2.opChamfer","BLEND_EDGE",EDGE,{"blendedFrom":[makeQuery(id+"F1.opExtrude","CAP_EDGE",EDGE,{"disambiguationData":[OSD([subQ0])],"isStart":false}),subQ1],"blendedInto":[subQ1]}),subQ1],"blendedInto":[subQ1]});}
            chamfer(context, id + "F4", {"entities" : qUnion([Q0, Q1, Q2, Q3, Q4, Q5, Q6, Q7, Q8, Q9, Q10, Q11, Q12, Q13]), "width" : 5 * mm, "tangentPropagation" : true});
        }
        {
            var Q0;
            {var subQ0=sQuery(id+"F0.wireOp",EDGE,"E1.2.0");var subQ1=makeQuery(id+"F1.opExtrude","CAP_FACE",FACE,{"disambiguationData":[OSD([sQuery(id+"F0.wireOp",EDGE,"E0"),sQuery(id+"F0.wireOp",EDGE,"E1.1.0"),subQ0,sQuery(id+"F0.wireOp",EDGE,"E1.3.0"),sQuery(id+"F0.wireOp",EDGE,"E1.4.0"),sQuery(id+"F0.wireOp",EDGE,"E1.5.0"),sQuery(id+"F0.wireOp",EDGE,"E1.6.0"),sQuery(id+"F0.wireOp",EDGE,"E1.7.0"),sQuery(id+"F0.wireOp",EDGE,"E1.8.0"),sQuery(id+"F0.wireOp",EDGE,"E1.9.0"),sQuery(id+"F0.wireOp",EDGE,"E2.1.10.0"),sQuery(id+"F0.wireOp",EDGE,"E2.1.11.0"),sQuery(id+"F0.wireOp",EDGE,"E3.1.12.0"),sQuery(id+"F0.wireOp",EDGE,"E3.1.13.0")])],"isStart":false});var subQ2=subQ1;Q0=makeQuery(id+"F4.opChamfer","BLEND_EDGE",EDGE,{"blendedFrom":[makeQuery(id+"F3.opChamfer","BLEND_EDGE",EDGE,{"blendedFrom":[makeQuery(id+"F2.opChamfer","BLEND_EDGE",EDGE,{"blendedFrom":[makeQuery(id+"F1.opExtrude","CAP_EDGE",EDGE,{"disambiguationData":[OSD([subQ0])],"isStart":false}),subQ1],"blendedInto":[subQ1]}),subQ2],"blendedInto":[subQ2]}),subQ2],"blendedInto":[subQ2]});}
            var Q1;
            {var subQ0=sQuery(id+"F0.wireOp",EDGE,"E1.3.0");var subQ1=makeQuery(id+"F1.opExtrude","CAP_FACE",FACE,{"disambiguationData":[OSD([sQuery(id+"F0.wireOp",EDGE,"E0"),sQuery(id+"F0.wireOp",EDGE,"E1.1.0"),sQuery(id+"F0.wireOp",EDGE,"E1.2.0"),subQ0,sQuery(id+"F0.wireOp",EDGE,"E1.4.0"),sQuery(id+"F0.wireOp",EDGE,"E1.5.0"),sQuery(id+"F0.wireOp",EDGE,"E1.6.0"),sQuery(id+"F0.wireOp",EDGE,"E1.7.0"),sQuery(id+"F0.wireOp",EDGE,"E1.8.0"),sQuery(id+"F0.wireOp",EDGE,"E1.9.0"),sQuery(id+"F0.wireOp",EDGE,"E2.1.10.0"),sQuery(id+"F0.wireOp",EDGE,"E2.1.11.0"),sQuery(id+"F0.wireOp",EDGE,"E3.1.12.0"),sQuery(id+"F0.wireOp",EDGE,"E3.1.13.0")])],"isStart":false});var subQ2=subQ1;Q1=makeQuery(id+"F4.opChamfer","BLEND_EDGE",EDGE,{"blendedFrom":[makeQuery(id+"F3.opChamfer","BLEND_EDGE",EDGE,{"blendedFrom":[makeQuery(id+"F2.opChamfer","BLEND_EDGE",EDGE,{"blendedFrom":[makeQuery(id+"F1.opExtrude","CAP_EDGE",EDGE,{"disambiguationData":[OSD([subQ0])],"isStart":false}),subQ1],"blendedInto":[subQ1]}),subQ2],"blendedInto":[subQ2]}),subQ2],"blendedInto":[subQ2]});}
            var Q2;
            {var subQ0=sQuery(id+"F0.wireOp",EDGE,"E1.4.0");var subQ1=makeQuery(id+"F1.opExtrude","CAP_FACE",FACE,{"disambiguationData":[OSD([sQuery(id+"F0.wireOp",EDGE,"E0"),sQuery(id+"F0.wireOp",EDGE,"E1.1.0"),sQuery(id+"F0.wireOp",EDGE,"E1.2.0"),sQuery(id+"F0.wireOp",EDGE,"E1.3.0"),subQ0,sQuery(id+"F0.wireOp",EDGE,"E1.5.0"),sQuery(id+"F0.wireOp",EDGE,"E1.6.0"),sQuery(id+"F0.wireOp",EDGE,"E1.7.0"),sQuery(id+"F0.wireOp",EDGE,"E1.8.0"),sQuery(id+"F0.wireOp",EDGE,"E1.9.0"),sQuery(id+"F0.wireOp",EDGE,"E2.1.10.0"),sQuery(id+"F0.wireOp",EDGE,"E2.1.11.0"),sQuery(id+"F0.wireOp",EDGE,"E3.1.12.0"),sQuery(id+"F0.wireOp",EDGE,"E3.1.13.0")])],"isStart":false});var subQ2=subQ1;Q2=makeQuery(id+"F4.opChamfer","BLEND_EDGE",EDGE,{"blendedFrom":[makeQuery(id+"F3.opChamfer","BLEND_EDGE",EDGE,{"blendedFrom":[makeQuery(id+"F2.opChamfer","BLEND_EDGE",EDGE,{"blendedFrom":[makeQuery(id+"F1.opExtrude","CAP_EDGE",EDGE,{"disambiguationData":[OSD([subQ0])],"isStart":false}),subQ1],"blendedInto":[subQ1]}),subQ2],"blendedInto":[subQ2]}),subQ2],"blendedInto":[subQ2]});}
            var Q3;
            {var subQ0=sQuery(id+"F0.wireOp",EDGE,"E1.5.0");var subQ1=makeQuery(id+"F1.opExtrude","CAP_FACE",FACE,{"disambiguationData":[OSD([sQuery(id+"F0.wireOp",EDGE,"E0"),sQuery(id+"F0.wireOp",EDGE,"E1.1.0"),sQuery(id+"F0.wireOp",EDGE,"E1.2.0"),sQuery(id+"F0.wireOp",EDGE,"E1.3.0"),sQuery(id+"F0.wireOp",EDGE,"E1.4.0"),subQ0,sQuery(id+"F0.wireOp",EDGE,"E1.6.0"),sQuery(id+"F0.wireOp",EDGE,"E1.7.0"),sQuery(id+"F0.wireOp",EDGE,"E1.8.0"),sQuery(id+"F0.wireOp",EDGE,"E1.9.0"),sQuery(id+"F0.wireOp",EDGE,"E2.1.10.0"),sQuery(id+"F0.wireOp",EDGE,"E2.1.11.0"),sQuery(id+"F0.wireOp",EDGE,"E3.1.12.0"),sQuery(id+"F0.wireOp",EDGE,"E3.1.13.0")])],"isStart":false});var subQ2=subQ1;Q3=makeQuery(id+"F4.opChamfer","BLEND_EDGE",EDGE,{"blendedFrom":[makeQuery(id+"F3.opChamfer","BLEND_EDGE",EDGE,{"blendedFrom":[makeQuery(id+"F2.opChamfer","BLEND_EDGE",EDGE,{"blendedFrom":[makeQuery(id+"F1.opExtrude","CAP_EDGE",EDGE,{"disambiguationData":[OSD([subQ0])],"isStart":false}),subQ1],"blendedInto":[subQ1]}),subQ2],"blendedInto":[subQ2]}),subQ2],"blendedInto":[subQ2]});}
            var Q4;
            {var subQ0=sQuery(id+"F0.wireOp",EDGE,"E1.6.0");var subQ1=makeQuery(id+"F1.opExtrude","CAP_FACE",FACE,{"disambiguationData":[OSD([sQuery(id+"F0.wireOp",EDGE,"E0"),sQuery(id+"F0.wireOp",EDGE,"E1.1.0"),sQuery(id+"F0.wireOp",EDGE,"E1.2.0"),sQuery(id+"F0.wireOp",EDGE,"E1.3.0"),sQuery(id+"F0.wireOp",EDGE,"E1.4.0"),sQuery(id+"F0.wireOp",EDGE,"E1.5.0"),subQ0,sQuery(id+"F0.wireOp",EDGE,"E1.7.0"),sQuery(id+"F0.wireOp",EDGE,"E1.8.0"),sQuery(id+"F0.wireOp",EDGE,"E1.9.0"),sQuery(id+"F0.wireOp",EDGE,"E2.1.10.0"),sQuery(id+"F0.wireOp",EDGE,"E2.1.11.0"),sQuery(id+"F0.wireOp",EDGE,"E3.1.12.0"),sQuery(id+"F0.wireOp",EDGE,"E3.1.13.0")])],"isStart":false});var subQ2=subQ1;Q4=makeQuery(id+"F4.opChamfer","BLEND_EDGE",EDGE,{"blendedFrom":[makeQuery(id+"F3.opChamfer","BLEND_EDGE",EDGE,{"blendedFrom":[makeQuery(id+"F2.opChamfer","BLEND_EDGE",EDGE,{"blendedFrom":[makeQuery(id+"F1.opExtrude","CAP_EDGE",EDGE,{"disambiguationData":[OSD([subQ0])],"isStart":false}),subQ1],"blendedInto":[subQ1]}),subQ2],"blendedInto":[subQ2]}),subQ2],"blendedInto":[subQ2]});}
            var Q5;
            {var subQ0=sQuery(id+"F0.wireOp",EDGE,"E1.7.0");var subQ1=makeQuery(id+"F1.opExtrude","CAP_FACE",FACE,{"disambiguationData":[OSD([sQuery(id+"F0.wireOp",EDGE,"E0"),sQuery(id+"F0.wireOp",EDGE,"E1.1.0"),sQuery(id+"F0.wireOp",EDGE,"E1.2.0"),sQuery(id+"F0.wireOp",EDGE,"E1.3.0"),sQuery(id+"F0.wireOp",EDGE,"E1.4.0"),sQuery(id+"F0.wireOp",EDGE,"E1.5.0"),sQuery(id+"F0.wireOp",EDGE,"E1.6.0"),subQ0,sQuery(id+"F0.wireOp",EDGE,"E1.8.0"),sQuery(id+"F0.wireOp",EDGE,"E1.9.0"),sQuery(id+"F0.wireOp",EDGE,"E2.1.10.0"),sQuery(id+"F0.wireOp",EDGE,"E2.1.11.0"),sQuery(id+"F0.wireOp",EDGE,"E3.1.12.0"),sQuery(id+"F0.wireOp",EDGE,"E3.1.13.0")])],"isStart":false});var subQ2=subQ1;Q5=makeQuery(id+"F4.opChamfer","BLEND_EDGE",EDGE,{"blendedFrom":[makeQuery(id+"F3.opChamfer","BLEND_EDGE",EDGE,{"blendedFrom":[makeQuery(id+"F2.opChamfer","BLEND_EDGE",EDGE,{"blendedFrom":[makeQuery(id+"F1.opExtrude","CAP_EDGE",EDGE,{"disambiguationData":[OSD([subQ0])],"isStart":false}),subQ1],"blendedInto":[subQ1]}),subQ2],"blendedInto":[subQ2]}),subQ2],"blendedInto":[subQ2]});}
            var Q6;
            {var subQ0=sQuery(id+"F0.wireOp",EDGE,"E1.8.0");var subQ1=makeQuery(id+"F1.opExtrude","CAP_FACE",FACE,{"disambiguationData":[OSD([sQuery(id+"F0.wireOp",EDGE,"E0"),sQuery(id+"F0.wireOp",EDGE,"E1.1.0"),sQuery(id+"F0.wireOp",EDGE,"E1.2.0"),sQuery(id+"F0.wireOp",EDGE,"E1.3.0"),sQuery(id+"F0.wireOp",EDGE,"E1.4.0"),sQuery(id+"F0.wireOp",EDGE,"E1.5.0"),sQuery(id+"F0.wireOp",EDGE,"E1.6.0"),sQuery(id+"F0.wireOp",EDGE,"E1.7.0"),subQ0,sQuery(id+"F0.wireOp",EDGE,"E1.9.0"),sQuery(id+"F0.wireOp",EDGE,"E2.1.10.0"),sQuery(id+"F0.wireOp",EDGE,"E2.1.11.0"),sQuery(id+"F0.wireOp",EDGE,"E3.1.12.0"),sQuery(id+"F0.wireOp",EDGE,"E3.1.13.0")])],"isStart":false});var subQ2=subQ1;Q6=makeQuery(id+"F4.opChamfer","BLEND_EDGE",EDGE,{"blendedFrom":[makeQuery(id+"F3.opChamfer","BLEND_EDGE",EDGE,{"blendedFrom":[makeQuery(id+"F2.opChamfer","BLEND_EDGE",EDGE,{"blendedFrom":[makeQuery(id+"F1.opExtrude","CAP_EDGE",EDGE,{"disambiguationData":[OSD([subQ0])],"isStart":false}),subQ1],"blendedInto":[subQ1]}),subQ2],"blendedInto":[subQ2]}),subQ2],"blendedInto":[subQ2]});}
            var Q7;
            {var subQ0=sQuery(id+"F0.wireOp",EDGE,"E1.9.0");var subQ1=makeQuery(id+"F1.opExtrude","CAP_FACE",FACE,{"disambiguationData":[OSD([sQuery(id+"F0.wireOp",EDGE,"E0"),sQuery(id+"F0.wireOp",EDGE,"E1.1.0"),sQuery(id+"F0.wireOp",EDGE,"E1.2.0"),sQuery(id+"F0.wireOp",EDGE,"E1.3.0"),sQuery(id+"F0.wireOp",EDGE,"E1.4.0"),sQuery(id+"F0.wireOp",EDGE,"E1.5.0"),sQuery(id+"F0.wireOp",EDGE,"E1.6.0"),sQuery(id+"F0.wireOp",EDGE,"E1.7.0"),sQuery(id+"F0.wireOp",EDGE,"E1.8.0"),subQ0,sQuery(id+"F0.wireOp",EDGE,"E2.1.10.0"),sQuery(id+"F0.wireOp",EDGE,"E2.1.11.0"),sQuery(id+"F0.wireOp",EDGE,"E3.1.12.0"),sQuery(id+"F0.wireOp",EDGE,"E3.1.13.0")])],"isStart":false});var subQ2=subQ1;Q7=makeQuery(id+"F4.opChamfer","BLEND_EDGE",EDGE,{"blendedFrom":[makeQuery(id+"F3.opChamfer","BLEND_EDGE",EDGE,{"blendedFrom":[makeQuery(id+"F2.opChamfer","BLEND_EDGE",EDGE,{"blendedFrom":[makeQuery(id+"F1.opExtrude","CAP_EDGE",EDGE,{"disambiguationData":[OSD([subQ0])],"isStart":false}),subQ1],"blendedInto":[subQ1]}),subQ2],"blendedInto":[subQ2]}),subQ2],"blendedInto":[subQ2]});}
            var Q8;
            Q8=makeQuery(id+"F1.opExtrude","CAP_FACE",FACE,{"disambiguationData":[OSD([sQuery(id+"F0.wireOp",EDGE,"E0"),sQuery(id+"F0.wireOp",EDGE,"E1.1.0"),sQuery(id+"F0.wireOp",EDGE,"E1.2.0"),sQuery(id+"F0.wireOp",EDGE,"E1.3.0"),sQuery(id+"F0.wireOp",EDGE,"E1.4.0"),sQuery(id+"F0.wireOp",EDGE,"E1.5.0"),sQuery(id+"F0.wireOp",EDGE,"E1.6.0"),sQuery(id+"F0.wireOp",EDGE,"E1.7.0"),sQuery(id+"F0.wireOp",EDGE,"E1.8.0"),sQuery(id+"F0.wireOp",EDGE,"E1.9.0"),sQuery(id+"F0.wireOp",EDGE,"E2.1.10.0"),sQuery(id+"F0.wireOp",EDGE,"E2.1.11.0"),sQuery(id+"F0.wireOp",EDGE,"E3.1.12.0"),sQuery(id+"F0.wireOp",EDGE,"E3.1.13.0")])],"isStart":false});
            chamfer(context, id + "F5", {"entities" : qUnion([Q0, Q1, Q2, Q3, Q4, Q5, Q6, Q7, Q8]), "width" : 5 * mm, "tangentPropagation" : true});
        }
        {
            var Q0;
            Q0=makeQuery(id+"F1.opExtrude","CAP_FACE",FACE,{"disambiguationData":[OSD([sQuery(id+"F0.wireOp",EDGE,"E0"),sQuery(id+"F0.wireOp",EDGE,"E1.1.0"),sQuery(id+"F0.wireOp",EDGE,"E1.2.0"),sQuery(id+"F0.wireOp",EDGE,"E1.3.0"),sQuery(id+"F0.wireOp",EDGE,"E1.4.0"),sQuery(id+"F0.wireOp",EDGE,"E1.5.0"),sQuery(id+"F0.wireOp",EDGE,"E1.6.0"),sQuery(id+"F0.wireOp",EDGE,"E1.7.0"),sQuery(id+"F0.wireOp",EDGE,"E1.8.0"),sQuery(id+"F0.wireOp",EDGE,"E1.9.0"),sQuery(id+"F0.wireOp",EDGE,"E2.1.10.0"),sQuery(id+"F0.wireOp",EDGE,"E2.1.11.0"),sQuery(id+"F0.wireOp",EDGE,"E3.1.12.0"),sQuery(id+"F0.wireOp",EDGE,"E3.1.13.0")])],"isStart":false});
            chamfer(context, id + "F6", {"entities" : qUnion([Q0]), "width" : 5 * mm, "tangentPropagation" : true});
        }
        {
            var Q0;
            Q0=makeQuery(id+"F1.opExtrude","CAP_FACE",FACE,{"disambiguationData":[OSD([sQuery(id+"F0.wireOp",EDGE,"E0"),sQuery(id+"F0.wireOp",EDGE,"E1.1.0"),sQuery(id+"F0.wireOp",EDGE,"E1.2.0"),sQuery(id+"F0.wireOp",EDGE,"E1.3.0"),sQuery(id+"F0.wireOp",EDGE,"E1.4.0"),sQuery(id+"F0.wireOp",EDGE,"E1.5.0"),sQuery(id+"F0.wireOp",EDGE,"E1.6.0"),sQuery(id+"F0.wireOp",EDGE,"E1.7.0"),sQuery(id+"F0.wireOp",EDGE,"E1.8.0"),sQuery(id+"F0.wireOp",EDGE,"E1.9.0"),sQuery(id+"F0.wireOp",EDGE,"E2.1.10.0"),sQuery(id+"F0.wireOp",EDGE,"E2.1.11.0"),sQuery(id+"F0.wireOp",EDGE,"E3.1.12.0"),sQuery(id+"F0.wireOp",EDGE,"E3.1.13.0")])],"isStart":false});
            chamfer(context, id + "F7", {"entities" : qUnion([Q0]), "width" : 5 * mm, "tangentPropagation" : true});
        }
        {
            var Q0;
            Q0=makeQuery(id+"F1.opExtrude","CAP_EDGE",EDGE,{"disambiguationData":[OSD([sQuery(id+"F0.wireOp",EDGE,"E1.4.0")])],"isStart":true});
            var Q1;
            Q1=makeQuery(id+"F1.opExtrude","CAP_FACE",FACE,{"disambiguationData":[OSD([sQuery(id+"F0.wireOp",EDGE,"E0"),sQuery(id+"F0.wireOp",EDGE,"E1.1.0"),sQuery(id+"F0.wireOp",EDGE,"E1.2.0"),sQuery(id+"F0.wireOp",EDGE,"E1.3.0"),sQuery(id+"F0.wireOp",EDGE,"E1.4.0"),sQuery(id+"F0.wireOp",EDGE,"E1.5.0"),sQuery(id+"F0.wireOp",EDGE,"E1.6.0"),sQuery(id+"F0.wireOp",EDGE,"E1.7.0"),sQuery(id+"F0.wireOp",EDGE,"E1.8.0"),sQuery(id+"F0.wireOp",EDGE,"E1.9.0"),sQuery(id+"F0.wireOp",EDGE,"E2.1.10.0"),sQuery(id+"F0.wireOp",EDGE,"E2.1.11.0"),sQuery(id+"F0.wireOp",EDGE,"E3.1.12.0"),sQuery(id+"F0.wireOp",EDGE,"E3.1.13.0")])],"isStart":true});
            chamfer(context, id + "F8", {"entities" : qUnion([Q0, Q1]), "width" : 5 * mm, "tangentPropagation" : true});
        }
        {
            var Q0;
            Q0=makeQuery(id+"F1.opExtrude","CAP_FACE",FACE,{"disambiguationData":[OSD([sQuery(id+"F0.wireOp",EDGE,"E0"),sQuery(id+"F0.wireOp",EDGE,"E1.1.0"),sQuery(id+"F0.wireOp",EDGE,"E1.2.0"),sQuery(id+"F0.wireOp",EDGE,"E1.3.0"),sQuery(id+"F0.wireOp",EDGE,"E1.4.0"),sQuery(id+"F0.wireOp",EDGE,"E1.5.0"),sQuery(id+"F0.wireOp",EDGE,"E1.6.0"),sQuery(id+"F0.wireOp",EDGE,"E1.7.0"),sQuery(id+"F0.wireOp",EDGE,"E1.8.0"),sQuery(id+"F0.wireOp",EDGE,"E1.9.0"),sQuery(id+"F0.wireOp",EDGE,"E2.1.10.0"),sQuery(id+"F0.wireOp",EDGE,"E2.1.11.0"),sQuery(id+"F0.wireOp",EDGE,"E3.1.12.0"),sQuery(id+"F0.wireOp",EDGE,"E3.1.13.0")])],"isStart":true});
            chamfer(context, id + "F9", {"entities" : qUnion([Q0]), "width" : 5 * mm, "tangentPropagation" : true});
        }
        {
            var Q0;
            Q0=makeQuery(id+"F1.opExtrude","CAP_FACE",FACE,{"disambiguationData":[OSD([sQuery(id+"F0.wireOp",EDGE,"E0"),sQuery(id+"F0.wireOp",EDGE,"E1.1.0"),sQuery(id+"F0.wireOp",EDGE,"E1.2.0"),sQuery(id+"F0.wireOp",EDGE,"E1.3.0"),sQuery(id+"F0.wireOp",EDGE,"E1.4.0"),sQuery(id+"F0.wireOp",EDGE,"E1.5.0"),sQuery(id+"F0.wireOp",EDGE,"E1.6.0"),sQuery(id+"F0.wireOp",EDGE,"E1.7.0"),sQuery(id+"F0.wireOp",EDGE,"E1.8.0"),sQuery(id+"F0.wireOp",EDGE,"E1.9.0"),sQuery(id+"F0.wireOp",EDGE,"E2.1.10.0"),sQuery(id+"F0.wireOp",EDGE,"E2.1.11.0"),sQuery(id+"F0.wireOp",EDGE,"E3.1.12.0"),sQuery(id+"F0.wireOp",EDGE,"E3.1.13.0")])],"isStart":true});
            chamfer(context, id + "F10", {"entities" : qUnion([Q0]), "width" : 5 * mm, "tangentPropagation" : true});
        }
        {
            var Q0;
            Q0=makeQuery(id+"F1.opExtrude","CAP_FACE",FACE,{"disambiguationData":[OSD([sQuery(id+"F0.wireOp",EDGE,"E0"),sQuery(id+"F0.wireOp",EDGE,"E1.1.0"),sQuery(id+"F0.wireOp",EDGE,"E1.2.0"),sQuery(id+"F0.wireOp",EDGE,"E1.3.0"),sQuery(id+"F0.wireOp",EDGE,"E1.4.0"),sQuery(id+"F0.wireOp",EDGE,"E1.5.0"),sQuery(id+"F0.wireOp",EDGE,"E1.6.0"),sQuery(id+"F0.wireOp",EDGE,"E1.7.0"),sQuery(id+"F0.wireOp",EDGE,"E1.8.0"),sQuery(id+"F0.wireOp",EDGE,"E1.9.0"),sQuery(id+"F0.wireOp",EDGE,"E2.1.10.0"),sQuery(id+"F0.wireOp",EDGE,"E2.1.11.0"),sQuery(id+"F0.wireOp",EDGE,"E3.1.12.0"),sQuery(id+"F0.wireOp",EDGE,"E3.1.13.0")])],"isStart":true});
            extrude(context, id + "F11", {"entities" : qUnion([Q0]), "operationType" : NewBodyOperationType.ADD, "depth" : 25 * mm, "offsetDistance" : 25 * mm});
        }
        {
            var Q0;
            Q0=makeQuery(id+"F1.opExtrude","CAP_FACE",FACE,{"disambiguationData":[OSD([sQuery(id+"F0.wireOp",EDGE,"E0"),sQuery(id+"F0.wireOp",EDGE,"E1.1.0"),sQuery(id+"F0.wireOp",EDGE,"E1.2.0"),sQuery(id+"F0.wireOp",EDGE,"E1.3.0"),sQuery(id+"F0.wireOp",EDGE,"E1.4.0"),sQuery(id+"F0.wireOp",EDGE,"E1.5.0"),sQuery(id+"F0.wireOp",EDGE,"E1.6.0"),sQuery(id+"F0.wireOp",EDGE,"E1.7.0"),sQuery(id+"F0.wireOp",EDGE,"E1.8.0"),sQuery(id+"F0.wireOp",EDGE,"E1.9.0"),sQuery(id+"F0.wireOp",EDGE,"E2.1.10.0"),sQuery(id+"F0.wireOp",EDGE,"E2.1.11.0"),sQuery(id+"F0.wireOp",EDGE,"E3.1.12.0"),sQuery(id+"F0.wireOp",EDGE,"E3.1.13.0")])],"isStart":false});
            extrude(context, id + "F12", {"entities" : qUnion([Q0]), "operationType" : NewBodyOperationType.ADD, "depth" : 10 * mm, "offsetDistance" : 25 * mm});
        }
        {
            var Q0;
            {var subQ0=sQuery(id+"F0.wireOp",EDGE,"E3.1.13.0");var subQ1=sQuery(id+"F0.wireOp",EDGE,"E3.1.12.0");var subQ2=sQuery(id+"F0.wireOp",EDGE,"E2.1.11.0");var subQ3=sQuery(id+"F0.wireOp",EDGE,"E2.1.10.0");var subQ4=sQuery(id+"F0.wireOp",EDGE,"E1.9.0");var subQ5=sQuery(id+"F0.wireOp",EDGE,"E1.8.0");var subQ6=sQuery(id+"F0.wireOp",EDGE,"E1.7.0");var subQ7=sQuery(id+"F0.wireOp",EDGE,"E1.6.0");var subQ8=sQuery(id+"F0.wireOp",EDGE,"E1.5.0");var subQ9=sQuery(id+"F0.wireOp",EDGE,"E1.4.0");var subQ10=sQuery(id+"F0.wireOp",EDGE,"E1.3.0");var subQ11=sQuery(id+"F0.wireOp",EDGE,"E1.2.0");var subQ12=sQuery(id+"F0.wireOp",EDGE,"E1.1.0");var subQ13=sQuery(id+"F0.wireOp",EDGE,"E0");var subQ14=makeQuery(id+"F1.opExtrude","CAP_FACE",FACE,{"disambiguationData":[OSD([subQ13,subQ12,subQ11,subQ10,subQ9,subQ8,subQ7,subQ6,subQ5,subQ4,subQ3,subQ2,subQ1,subQ0])],"isStart":false});var subQ15=subQ14;var subQ16=subQ15;var subQ17=subQ16;var subQ18=subQ17;Q0=makeQuery(id+"F12.opExtrude","CAP_EDGE",EDGE,{"disambiguationData":[OSD([subQ13,subQ12,subQ11,subQ10,subQ9,subQ8,subQ7,subQ6,subQ5,subQ4,subQ3,subQ2,subQ1,subQ0]),TDD([makeQuery(id+"F7.opChamfer","BLEND_EDGE",EDGE,{"blendedFrom":[makeQuery(id+"F6.opChamfer","BLEND_EDGE",EDGE,{"blendedFrom":[makeQuery(id+"F5.opChamfer","BLEND_EDGE",EDGE,{"blendedFrom":[makeQuery(id+"F4.opChamfer","BLEND_EDGE",EDGE,{"blendedFrom":[makeQuery(id+"F3.opChamfer","BLEND_EDGE",EDGE,{"blendedFrom":[makeQuery(id+"F2.opChamfer","BLEND_EDGE",EDGE,{"blendedFrom":[makeQuery(id+"F1.opExtrude","CAP_EDGE",EDGE,{"disambiguationData":[OSD([subQ12])],"isStart":false}),subQ14],"blendedInto":[subQ14]}),subQ15],"blendedInto":[subQ15]}),subQ16],"blendedInto":[subQ16]}),subQ17],"blendedInto":[subQ17]}),subQ18],"blendedInto":[subQ18]}),subQ18],"blendedInto":[subQ18]})])],"isStart":false});}
            var Q1;
            {var subQ0=sQuery(id+"F0.wireOp",EDGE,"E3.1.13.0");var subQ1=sQuery(id+"F0.wireOp",EDGE,"E3.1.12.0");var subQ2=sQuery(id+"F0.wireOp",EDGE,"E2.1.11.0");var subQ3=sQuery(id+"F0.wireOp",EDGE,"E2.1.10.0");var subQ4=sQuery(id+"F0.wireOp",EDGE,"E1.9.0");var subQ5=sQuery(id+"F0.wireOp",EDGE,"E1.8.0");var subQ6=sQuery(id+"F0.wireOp",EDGE,"E1.7.0");var subQ7=sQuery(id+"F0.wireOp",EDGE,"E1.6.0");var subQ8=sQuery(id+"F0.wireOp",EDGE,"E1.5.0");var subQ9=sQuery(id+"F0.wireOp",EDGE,"E1.4.0");var subQ10=sQuery(id+"F0.wireOp",EDGE,"E1.3.0");var subQ11=sQuery(id+"F0.wireOp",EDGE,"E1.2.0");var subQ12=sQuery(id+"F0.wireOp",EDGE,"E1.1.0");var subQ13=sQuery(id+"F0.wireOp",EDGE,"E0");var subQ14=makeQuery(id+"F1.opExtrude","CAP_FACE",FACE,{"disambiguationData":[OSD([subQ13,subQ12,subQ11,subQ10,subQ9,subQ8,subQ7,subQ6,subQ5,subQ4,subQ3,subQ2,subQ1,subQ0])],"isStart":false});var subQ15=subQ14;var subQ16=subQ15;var subQ17=subQ16;var subQ18=subQ17;Q1=makeQuery(id+"F12.opExtrude","CAP_EDGE",EDGE,{"disambiguationData":[OSD([subQ13,subQ12,subQ11,subQ10,subQ9,subQ8,subQ7,subQ6,subQ5,subQ4,subQ3,subQ2,subQ1,subQ0]),TDD([makeQuery(id+"F7.opChamfer","BLEND_EDGE",EDGE,{"blendedFrom":[makeQuery(id+"F6.opChamfer","BLEND_EDGE",EDGE,{"blendedFrom":[makeQuery(id+"F5.opChamfer","BLEND_EDGE",EDGE,{"blendedFrom":[makeQuery(id+"F4.opChamfer","BLEND_EDGE",EDGE,{"blendedFrom":[makeQuery(id+"F3.opChamfer","BLEND_EDGE",EDGE,{"blendedFrom":[makeQuery(id+"F2.opChamfer","BLEND_EDGE",EDGE,{"blendedFrom":[makeQuery(id+"F1.opExtrude","CAP_EDGE",EDGE,{"disambiguationData":[OSD([subQ6])],"isStart":false}),subQ14],"blendedInto":[subQ14]}),subQ15],"blendedInto":[subQ15]}),subQ16],"blendedInto":[subQ16]}),subQ17],"blendedInto":[subQ17]}),subQ18],"blendedInto":[subQ18]}),subQ18],"blendedInto":[subQ18]})])],"isStart":false});}
            var Q2;
            {var subQ0=sQuery(id+"F0.wireOp",EDGE,"E3.1.13.0");var subQ1=sQuery(id+"F0.wireOp",EDGE,"E3.1.12.0");var subQ2=sQuery(id+"F0.wireOp",EDGE,"E2.1.11.0");var subQ3=sQuery(id+"F0.wireOp",EDGE,"E2.1.10.0");var subQ4=sQuery(id+"F0.wireOp",EDGE,"E1.9.0");var subQ5=sQuery(id+"F0.wireOp",EDGE,"E1.8.0");var subQ6=sQuery(id+"F0.wireOp",EDGE,"E1.7.0");var subQ7=sQuery(id+"F0.wireOp",EDGE,"E1.6.0");var subQ8=sQuery(id+"F0.wireOp",EDGE,"E1.5.0");var subQ9=sQuery(id+"F0.wireOp",EDGE,"E1.4.0");var subQ10=sQuery(id+"F0.wireOp",EDGE,"E1.3.0");var subQ11=sQuery(id+"F0.wireOp",EDGE,"E1.2.0");var subQ12=sQuery(id+"F0.wireOp",EDGE,"E1.1.0");var subQ13=sQuery(id+"F0.wireOp",EDGE,"E0");var subQ14=makeQuery(id+"F1.opExtrude","CAP_FACE",FACE,{"disambiguationData":[OSD([subQ13,subQ12,subQ11,subQ10,subQ9,subQ8,subQ7,subQ6,subQ5,subQ4,subQ3,subQ2,subQ1,subQ0])],"isStart":false});var subQ15=subQ14;var subQ16=subQ15;var subQ17=subQ16;var subQ18=subQ17;Q2=makeQuery(id+"F12.opExtrude","CAP_EDGE",EDGE,{"disambiguationData":[OSD([subQ13,subQ12,subQ11,subQ10,subQ9,subQ8,subQ7,subQ6,subQ5,subQ4,subQ3,subQ2,subQ1,subQ0]),TDD([makeQuery(id+"F7.opChamfer","BLEND_EDGE",EDGE,{"blendedFrom":[makeQuery(id+"F6.opChamfer","BLEND_EDGE",EDGE,{"blendedFrom":[makeQuery(id+"F5.opChamfer","BLEND_EDGE",EDGE,{"blendedFrom":[makeQuery(id+"F4.opChamfer","BLEND_EDGE",EDGE,{"blendedFrom":[makeQuery(id+"F3.opChamfer","BLEND_EDGE",EDGE,{"blendedFrom":[makeQuery(id+"F2.opChamfer","BLEND_EDGE",EDGE,{"blendedFrom":[makeQuery(id+"F1.opExtrude","CAP_EDGE",EDGE,{"disambiguationData":[OSD([subQ4])],"isStart":false}),subQ14],"blendedInto":[subQ14]}),subQ15],"blendedInto":[subQ15]}),subQ16],"blendedInto":[subQ16]}),subQ17],"blendedInto":[subQ17]}),subQ18],"blendedInto":[subQ18]}),subQ18],"blendedInto":[subQ18]})])],"isStart":false});}
            var Q3;
            {var subQ0=sQuery(id+"F0.wireOp",EDGE,"E3.1.13.0");var subQ1=sQuery(id+"F0.wireOp",EDGE,"E3.1.12.0");var subQ2=sQuery(id+"F0.wireOp",EDGE,"E2.1.11.0");var subQ3=sQuery(id+"F0.wireOp",EDGE,"E2.1.10.0");var subQ4=sQuery(id+"F0.wireOp",EDGE,"E1.9.0");var subQ5=sQuery(id+"F0.wireOp",EDGE,"E1.8.0");var subQ6=sQuery(id+"F0.wireOp",EDGE,"E1.7.0");var subQ7=sQuery(id+"F0.wireOp",EDGE,"E1.6.0");var subQ8=sQuery(id+"F0.wireOp",EDGE,"E1.5.0");var subQ9=sQuery(id+"F0.wireOp",EDGE,"E1.4.0");var subQ10=sQuery(id+"F0.wireOp",EDGE,"E1.3.0");var subQ11=sQuery(id+"F0.wireOp",EDGE,"E1.2.0");var subQ12=sQuery(id+"F0.wireOp",EDGE,"E1.1.0");var subQ13=sQuery(id+"F0.wireOp",EDGE,"E0");var subQ14=makeQuery(id+"F1.opExtrude","CAP_FACE",FACE,{"disambiguationData":[OSD([subQ13,subQ12,subQ11,subQ10,subQ9,subQ8,subQ7,subQ6,subQ5,subQ4,subQ3,subQ2,subQ1,subQ0])],"isStart":false});var subQ15=subQ14;var subQ16=subQ15;var subQ17=subQ16;var subQ18=subQ17;Q3=makeQuery(id+"F12.opExtrude","CAP_EDGE",EDGE,{"disambiguationData":[OSD([subQ13,subQ12,subQ11,subQ10,subQ9,subQ8,subQ7,subQ6,subQ5,subQ4,subQ3,subQ2,subQ1,subQ0]),TDD([makeQuery(id+"F7.opChamfer","BLEND_EDGE",EDGE,{"blendedFrom":[makeQuery(id+"F6.opChamfer","BLEND_EDGE",EDGE,{"blendedFrom":[makeQuery(id+"F5.opChamfer","BLEND_EDGE",EDGE,{"blendedFrom":[makeQuery(id+"F4.opChamfer","BLEND_EDGE",EDGE,{"blendedFrom":[makeQuery(id+"F3.opChamfer","BLEND_EDGE",EDGE,{"blendedFrom":[makeQuery(id+"F2.opChamfer","BLEND_EDGE",EDGE,{"blendedFrom":[makeQuery(id+"F1.opExtrude","CAP_EDGE",EDGE,{"disambiguationData":[OSD([subQ2])],"isStart":false}),subQ14],"blendedInto":[subQ14]}),subQ15],"blendedInto":[subQ15]}),subQ16],"blendedInto":[subQ16]}),subQ17],"blendedInto":[subQ17]}),subQ18],"blendedInto":[subQ18]}),subQ18],"blendedInto":[subQ18]})])],"isStart":false});}
            var Q4;
            {var subQ0=sQuery(id+"F0.wireOp",EDGE,"E3.1.13.0");var subQ1=sQuery(id+"F0.wireOp",EDGE,"E3.1.12.0");var subQ2=sQuery(id+"F0.wireOp",EDGE,"E2.1.11.0");var subQ3=sQuery(id+"F0.wireOp",EDGE,"E2.1.10.0");var subQ4=sQuery(id+"F0.wireOp",EDGE,"E1.9.0");var subQ5=sQuery(id+"F0.wireOp",EDGE,"E1.8.0");var subQ6=sQuery(id+"F0.wireOp",EDGE,"E1.7.0");var subQ7=sQuery(id+"F0.wireOp",EDGE,"E1.6.0");var subQ8=sQuery(id+"F0.wireOp",EDGE,"E1.5.0");var subQ9=sQuery(id+"F0.wireOp",EDGE,"E1.4.0");var subQ10=sQuery(id+"F0.wireOp",EDGE,"E1.3.0");var subQ11=sQuery(id+"F0.wireOp",EDGE,"E1.2.0");var subQ12=sQuery(id+"F0.wireOp",EDGE,"E1.1.0");var subQ13=sQuery(id+"F0.wireOp",EDGE,"E0");var subQ14=makeQuery(id+"F1.opExtrude","CAP_FACE",FACE,{"disambiguationData":[OSD([subQ13,subQ12,subQ11,subQ10,subQ9,subQ8,subQ7,subQ6,subQ5,subQ4,subQ3,subQ2,subQ1,subQ0])],"isStart":false});var subQ15=subQ14;var subQ16=subQ15;var subQ17=subQ16;var subQ18=subQ17;Q4=makeQuery(id+"F12.opExtrude","CAP_EDGE",EDGE,{"disambiguationData":[OSD([subQ13,subQ12,subQ11,subQ10,subQ9,subQ8,subQ7,subQ6,subQ5,subQ4,subQ3,subQ2,subQ1,subQ0]),TDD([makeQuery(id+"F7.opChamfer","BLEND_EDGE",EDGE,{"blendedFrom":[makeQuery(id+"F6.opChamfer","BLEND_EDGE",EDGE,{"blendedFrom":[makeQuery(id+"F5.opChamfer","BLEND_EDGE",EDGE,{"blendedFrom":[makeQuery(id+"F4.opChamfer","BLEND_EDGE",EDGE,{"blendedFrom":[makeQuery(id+"F3.opChamfer","BLEND_EDGE",EDGE,{"blendedFrom":[makeQuery(id+"F2.opChamfer","BLEND_EDGE",EDGE,{"blendedFrom":[makeQuery(id+"F1.opExtrude","CAP_EDGE",EDGE,{"disambiguationData":[OSD([subQ0])],"isStart":false}),subQ14],"blendedInto":[subQ14]}),subQ15],"blendedInto":[subQ15]}),subQ16],"blendedInto":[subQ16]}),subQ17],"blendedInto":[subQ17]}),subQ18],"blendedInto":[subQ18]}),subQ18],"blendedInto":[subQ18]})])],"isStart":false});}
            var Q5;
            {var subQ0=sQuery(id+"F0.wireOp",EDGE,"E3.1.13.0");var subQ1=sQuery(id+"F0.wireOp",EDGE,"E3.1.12.0");var subQ2=sQuery(id+"F0.wireOp",EDGE,"E2.1.11.0");var subQ3=sQuery(id+"F0.wireOp",EDGE,"E2.1.10.0");var subQ4=sQuery(id+"F0.wireOp",EDGE,"E1.9.0");var subQ5=sQuery(id+"F0.wireOp",EDGE,"E1.8.0");var subQ6=sQuery(id+"F0.wireOp",EDGE,"E1.7.0");var subQ7=sQuery(id+"F0.wireOp",EDGE,"E1.6.0");var subQ8=sQuery(id+"F0.wireOp",EDGE,"E1.5.0");var subQ9=sQuery(id+"F0.wireOp",EDGE,"E1.4.0");var subQ10=sQuery(id+"F0.wireOp",EDGE,"E1.3.0");var subQ11=sQuery(id+"F0.wireOp",EDGE,"E1.2.0");var subQ12=sQuery(id+"F0.wireOp",EDGE,"E1.1.0");var subQ13=sQuery(id+"F0.wireOp",EDGE,"E0");var subQ14=makeQuery(id+"F1.opExtrude","CAP_FACE",FACE,{"disambiguationData":[OSD([subQ13,subQ12,subQ11,subQ10,subQ9,subQ8,subQ7,subQ6,subQ5,subQ4,subQ3,subQ2,subQ1,subQ0])],"isStart":false});var subQ15=subQ14;var subQ16=subQ15;var subQ17=subQ16;var subQ18=subQ17;Q5=makeQuery(id+"F12.opExtrude","CAP_EDGE",EDGE,{"disambiguationData":[OSD([subQ13,subQ12,subQ11,subQ10,subQ9,subQ8,subQ7,subQ6,subQ5,subQ4,subQ3,subQ2,subQ1,subQ0]),TDD([makeQuery(id+"F7.opChamfer","BLEND_EDGE",EDGE,{"blendedFrom":[makeQuery(id+"F6.opChamfer","BLEND_EDGE",EDGE,{"blendedFrom":[makeQuery(id+"F5.opChamfer","BLEND_EDGE",EDGE,{"blendedFrom":[makeQuery(id+"F4.opChamfer","BLEND_EDGE",EDGE,{"blendedFrom":[makeQuery(id+"F3.opChamfer","BLEND_EDGE",EDGE,{"blendedFrom":[makeQuery(id+"F2.opChamfer","BLEND_EDGE",EDGE,{"blendedFrom":[makeQuery(id+"F1.opExtrude","CAP_EDGE",EDGE,{"disambiguationData":[OSD([subQ10])],"isStart":false}),subQ14],"blendedInto":[subQ14]}),subQ15],"blendedInto":[subQ15]}),subQ16],"blendedInto":[subQ16]}),subQ17],"blendedInto":[subQ17]}),subQ18],"blendedInto":[subQ18]}),subQ18],"blendedInto":[subQ18]})])],"isStart":false});}
            var Q6;
            {var subQ0=sQuery(id+"F0.wireOp",EDGE,"E3.1.13.0");var subQ1=sQuery(id+"F0.wireOp",EDGE,"E3.1.12.0");var subQ2=sQuery(id+"F0.wireOp",EDGE,"E2.1.11.0");var subQ3=sQuery(id+"F0.wireOp",EDGE,"E2.1.10.0");var subQ4=sQuery(id+"F0.wireOp",EDGE,"E1.9.0");var subQ5=sQuery(id+"F0.wireOp",EDGE,"E1.8.0");var subQ6=sQuery(id+"F0.wireOp",EDGE,"E1.7.0");var subQ7=sQuery(id+"F0.wireOp",EDGE,"E1.6.0");var subQ8=sQuery(id+"F0.wireOp",EDGE,"E1.5.0");var subQ9=sQuery(id+"F0.wireOp",EDGE,"E1.4.0");var subQ10=sQuery(id+"F0.wireOp",EDGE,"E1.3.0");var subQ11=sQuery(id+"F0.wireOp",EDGE,"E1.2.0");var subQ12=sQuery(id+"F0.wireOp",EDGE,"E1.1.0");var subQ13=sQuery(id+"F0.wireOp",EDGE,"E0");var subQ14=makeQuery(id+"F1.opExtrude","CAP_FACE",FACE,{"disambiguationData":[OSD([subQ13,subQ12,subQ11,subQ10,subQ9,subQ8,subQ7,subQ6,subQ5,subQ4,subQ3,subQ2,subQ1,subQ0])],"isStart":false});var subQ15=subQ14;var subQ16=subQ15;var subQ17=subQ16;var subQ18=subQ17;Q6=makeQuery(id+"F12.opExtrude","CAP_EDGE",EDGE,{"disambiguationData":[OSD([subQ13,subQ12,subQ11,subQ10,subQ9,subQ8,subQ7,subQ6,subQ5,subQ4,subQ3,subQ2,subQ1,subQ0]),TDD([makeQuery(id+"F7.opChamfer","BLEND_EDGE",EDGE,{"blendedFrom":[makeQuery(id+"F6.opChamfer","BLEND_EDGE",EDGE,{"blendedFrom":[makeQuery(id+"F5.opChamfer","BLEND_EDGE",EDGE,{"blendedFrom":[makeQuery(id+"F4.opChamfer","BLEND_EDGE",EDGE,{"blendedFrom":[makeQuery(id+"F3.opChamfer","BLEND_EDGE",EDGE,{"blendedFrom":[makeQuery(id+"F2.opChamfer","BLEND_EDGE",EDGE,{"blendedFrom":[makeQuery(id+"F1.opExtrude","CAP_EDGE",EDGE,{"disambiguationData":[OSD([subQ8])],"isStart":false}),subQ14],"blendedInto":[subQ14]}),subQ15],"blendedInto":[subQ15]}),subQ16],"blendedInto":[subQ16]}),subQ17],"blendedInto":[subQ17]}),subQ18],"blendedInto":[subQ18]}),subQ18],"blendedInto":[subQ18]})])],"isStart":false});}
            chamfer(context, id + "F13", {"entities" : qUnion([Q0, Q1, Q2, Q3, Q4, Q5, Q6]), "width" : 5 * mm, "tangentPropagation" : true});
        }
        {
            var Q0;
            {var subQ0=sQuery(id+"F0.wireOp",EDGE,"E3.1.13.0");var subQ1=sQuery(id+"F0.wireOp",EDGE,"E3.1.12.0");var subQ2=sQuery(id+"F0.wireOp",EDGE,"E2.1.11.0");var subQ3=sQuery(id+"F0.wireOp",EDGE,"E2.1.10.0");var subQ4=sQuery(id+"F0.wireOp",EDGE,"E1.9.0");var subQ5=sQuery(id+"F0.wireOp",EDGE,"E1.8.0");var subQ6=sQuery(id+"F0.wireOp",EDGE,"E1.7.0");var subQ7=sQuery(id+"F0.wireOp",EDGE,"E1.6.0");var subQ8=sQuery(id+"F0.wireOp",EDGE,"E1.5.0");var subQ9=sQuery(id+"F0.wireOp",EDGE,"E1.4.0");var subQ10=sQuery(id+"F0.wireOp",EDGE,"E1.3.0");var subQ11=sQuery(id+"F0.wireOp",EDGE,"E1.2.0");var subQ12=sQuery(id+"F0.wireOp",EDGE,"E1.1.0");var subQ13=sQuery(id+"F0.wireOp",EDGE,"E0");var subQ14=makeQuery(id+"F1.opExtrude","CAP_FACE",FACE,{"disambiguationData":[OSD([subQ13,subQ12,subQ11,subQ10,subQ9,subQ8,subQ7,subQ6,subQ5,subQ4,subQ3,subQ2,subQ1,subQ0])],"isStart":true});var subQ15=subQ14;Q0=makeQuery(id+"F11.opExtrude","CAP_EDGE",EDGE,{"disambiguationData":[OSD([subQ13,subQ12,subQ11,subQ10,subQ9,subQ8,subQ7,subQ6,subQ5,subQ4,subQ3,subQ2,subQ1,subQ0]),TDD([makeQuery(id+"F10.opChamfer","BLEND_EDGE",EDGE,{"blendedFrom":[makeQuery(id+"F9.opChamfer","BLEND_EDGE",EDGE,{"blendedFrom":[makeQuery(id+"F8.opChamfer","BLEND_EDGE",EDGE,{"blendedFrom":[makeQuery(id+"F1.opExtrude","CAP_EDGE",EDGE,{"disambiguationData":[OSD([subQ8])],"isStart":true}),subQ14],"blendedInto":[subQ14]}),subQ15],"blendedInto":[subQ15]}),subQ15],"blendedInto":[subQ15]})])],"isStart":false});}
            var Q1;
            {var subQ0=sQuery(id+"F0.wireOp",EDGE,"E3.1.13.0");var subQ1=sQuery(id+"F0.wireOp",EDGE,"E3.1.12.0");var subQ2=sQuery(id+"F0.wireOp",EDGE,"E2.1.11.0");var subQ3=sQuery(id+"F0.wireOp",EDGE,"E2.1.10.0");var subQ4=sQuery(id+"F0.wireOp",EDGE,"E1.9.0");var subQ5=sQuery(id+"F0.wireOp",EDGE,"E1.8.0");var subQ6=sQuery(id+"F0.wireOp",EDGE,"E1.7.0");var subQ7=sQuery(id+"F0.wireOp",EDGE,"E1.6.0");var subQ8=sQuery(id+"F0.wireOp",EDGE,"E1.5.0");var subQ9=sQuery(id+"F0.wireOp",EDGE,"E1.4.0");var subQ10=sQuery(id+"F0.wireOp",EDGE,"E1.3.0");var subQ11=sQuery(id+"F0.wireOp",EDGE,"E1.2.0");var subQ12=sQuery(id+"F0.wireOp",EDGE,"E1.1.0");var subQ13=sQuery(id+"F0.wireOp",EDGE,"E0");var subQ14=makeQuery(id+"F1.opExtrude","CAP_FACE",FACE,{"disambiguationData":[OSD([subQ13,subQ12,subQ11,subQ10,subQ9,subQ8,subQ7,subQ6,subQ5,subQ4,subQ3,subQ2,subQ1,subQ0])],"isStart":true});var subQ15=subQ14;Q1=makeQuery(id+"F11.opExtrude","CAP_EDGE",EDGE,{"disambiguationData":[OSD([subQ13,subQ12,subQ11,subQ10,subQ9,subQ8,subQ7,subQ6,subQ5,subQ4,subQ3,subQ2,subQ1,subQ0]),TDD([makeQuery(id+"F10.opChamfer","BLEND_EDGE",EDGE,{"blendedFrom":[makeQuery(id+"F9.opChamfer","BLEND_EDGE",EDGE,{"blendedFrom":[makeQuery(id+"F8.opChamfer","BLEND_EDGE",EDGE,{"blendedFrom":[makeQuery(id+"F1.opExtrude","CAP_EDGE",EDGE,{"disambiguationData":[OSD([subQ7])],"isStart":true}),subQ14],"blendedInto":[subQ14]}),subQ15],"blendedInto":[subQ15]}),subQ15],"blendedInto":[subQ15]})])],"isStart":false});}
            var Q2;
            {var subQ0=sQuery(id+"F0.wireOp",EDGE,"E3.1.13.0");var subQ1=sQuery(id+"F0.wireOp",EDGE,"E3.1.12.0");var subQ2=sQuery(id+"F0.wireOp",EDGE,"E2.1.11.0");var subQ3=sQuery(id+"F0.wireOp",EDGE,"E2.1.10.0");var subQ4=sQuery(id+"F0.wireOp",EDGE,"E1.9.0");var subQ5=sQuery(id+"F0.wireOp",EDGE,"E1.8.0");var subQ6=sQuery(id+"F0.wireOp",EDGE,"E1.7.0");var subQ7=sQuery(id+"F0.wireOp",EDGE,"E1.6.0");var subQ8=sQuery(id+"F0.wireOp",EDGE,"E1.5.0");var subQ9=sQuery(id+"F0.wireOp",EDGE,"E1.4.0");var subQ10=sQuery(id+"F0.wireOp",EDGE,"E1.3.0");var subQ11=sQuery(id+"F0.wireOp",EDGE,"E1.2.0");var subQ12=sQuery(id+"F0.wireOp",EDGE,"E1.1.0");var subQ13=sQuery(id+"F0.wireOp",EDGE,"E0");var subQ14=makeQuery(id+"F1.opExtrude","CAP_FACE",FACE,{"disambiguationData":[OSD([subQ13,subQ12,subQ11,subQ10,subQ9,subQ8,subQ7,subQ6,subQ5,subQ4,subQ3,subQ2,subQ1,subQ0])],"isStart":true});var subQ15=subQ14;Q2=makeQuery(id+"F11.opExtrude","CAP_EDGE",EDGE,{"disambiguationData":[OSD([subQ13,subQ12,subQ11,subQ10,subQ9,subQ8,subQ7,subQ6,subQ5,subQ4,subQ3,subQ2,subQ1,subQ0]),TDD([makeQuery(id+"F10.opChamfer","BLEND_EDGE",EDGE,{"blendedFrom":[makeQuery(id+"F9.opChamfer","BLEND_EDGE",EDGE,{"blendedFrom":[makeQuery(id+"F8.opChamfer","BLEND_EDGE",EDGE,{"blendedFrom":[makeQuery(id+"F1.opExtrude","CAP_EDGE",EDGE,{"disambiguationData":[OSD([subQ6])],"isStart":true}),subQ14],"blendedInto":[subQ14]}),subQ15],"blendedInto":[subQ15]}),subQ15],"blendedInto":[subQ15]})])],"isStart":false});}
            var Q3;
            {var subQ0=sQuery(id+"F0.wireOp",EDGE,"E3.1.13.0");var subQ1=sQuery(id+"F0.wireOp",EDGE,"E3.1.12.0");var subQ2=sQuery(id+"F0.wireOp",EDGE,"E2.1.11.0");var subQ3=sQuery(id+"F0.wireOp",EDGE,"E2.1.10.0");var subQ4=sQuery(id+"F0.wireOp",EDGE,"E1.9.0");var subQ5=sQuery(id+"F0.wireOp",EDGE,"E1.8.0");var subQ6=sQuery(id+"F0.wireOp",EDGE,"E1.7.0");var subQ7=sQuery(id+"F0.wireOp",EDGE,"E1.6.0");var subQ8=sQuery(id+"F0.wireOp",EDGE,"E1.5.0");var subQ9=sQuery(id+"F0.wireOp",EDGE,"E1.4.0");var subQ10=sQuery(id+"F0.wireOp",EDGE,"E1.3.0");var subQ11=sQuery(id+"F0.wireOp",EDGE,"E1.2.0");var subQ12=sQuery(id+"F0.wireOp",EDGE,"E1.1.0");var subQ13=sQuery(id+"F0.wireOp",EDGE,"E0");var subQ14=makeQuery(id+"F1.opExtrude","CAP_FACE",FACE,{"disambiguationData":[OSD([subQ13,subQ12,subQ11,subQ10,subQ9,subQ8,subQ7,subQ6,subQ5,subQ4,subQ3,subQ2,subQ1,subQ0])],"isStart":true});var subQ15=subQ14;Q3=makeQuery(id+"F11.opExtrude","CAP_EDGE",EDGE,{"disambiguationData":[OSD([subQ13,subQ12,subQ11,subQ10,subQ9,subQ8,subQ7,subQ6,subQ5,subQ4,subQ3,subQ2,subQ1,subQ0]),TDD([makeQuery(id+"F10.opChamfer","BLEND_EDGE",EDGE,{"blendedFrom":[makeQuery(id+"F9.opChamfer","BLEND_EDGE",EDGE,{"blendedFrom":[makeQuery(id+"F8.opChamfer","BLEND_EDGE",EDGE,{"blendedFrom":[makeQuery(id+"F1.opExtrude","CAP_EDGE",EDGE,{"disambiguationData":[OSD([subQ5])],"isStart":true}),subQ14],"blendedInto":[subQ14]}),subQ15],"blendedInto":[subQ15]}),subQ15],"blendedInto":[subQ15]})])],"isStart":false});}
            var Q4;
            Q4=makeQuery(id+"F11.opExtrude","CAP_FACE",FACE,{"disambiguationData":[OSD([sQuery(id+"F0.wireOp",EDGE,"E0"),sQuery(id+"F0.wireOp",EDGE,"E1.1.0"),sQuery(id+"F0.wireOp",EDGE,"E1.2.0"),sQuery(id+"F0.wireOp",EDGE,"E1.3.0"),sQuery(id+"F0.wireOp",EDGE,"E1.4.0"),sQuery(id+"F0.wireOp",EDGE,"E1.5.0"),sQuery(id+"F0.wireOp",EDGE,"E1.6.0"),sQuery(id+"F0.wireOp",EDGE,"E1.7.0"),sQuery(id+"F0.wireOp",EDGE,"E1.8.0"),sQuery(id+"F0.wireOp",EDGE,"E1.9.0"),sQuery(id+"F0.wireOp",EDGE,"E2.1.10.0"),sQuery(id+"F0.wireOp",EDGE,"E2.1.11.0"),sQuery(id+"F0.wireOp",EDGE,"E3.1.12.0"),sQuery(id+"F0.wireOp",EDGE,"E3.1.13.0")])],"isStart":false});
            chamfer(context, id + "F14", {"entities" : qUnion([Q0, Q1, Q2, Q3, Q4]), "width" : 5 * mm, "tangentPropagation" : true});
        }
        {
            var Q0;
            Q0=makeQuery(id+"F11.opExtrude","CAP_FACE",FACE,{"disambiguationData":[OSD([sQuery(id+"F0.wireOp",EDGE,"E0"),sQuery(id+"F0.wireOp",EDGE,"E1.1.0"),sQuery(id+"F0.wireOp",EDGE,"E1.2.0"),sQuery(id+"F0.wireOp",EDGE,"E1.3.0"),sQuery(id+"F0.wireOp",EDGE,"E1.4.0"),sQuery(id+"F0.wireOp",EDGE,"E1.5.0"),sQuery(id+"F0.wireOp",EDGE,"E1.6.0"),sQuery(id+"F0.wireOp",EDGE,"E1.7.0"),sQuery(id+"F0.wireOp",EDGE,"E1.8.0"),sQuery(id+"F0.wireOp",EDGE,"E1.9.0"),sQuery(id+"F0.wireOp",EDGE,"E2.1.10.0"),sQuery(id+"F0.wireOp",EDGE,"E2.1.11.0"),sQuery(id+"F0.wireOp",EDGE,"E3.1.12.0"),sQuery(id+"F0.wireOp",EDGE,"E3.1.13.0")])],"isStart":false});
            extrude(context, id + "F15", {"entities" : qUnion([Q0]), "operationType" : NewBodyOperationType.ADD, "depth" : 25 * mm, "offsetDistance" : 25 * mm});
        }
        {
            var Q0;
            Q0=makeQuery(id+"F15.opExtrude","CAP_FACE",FACE,{"disambiguationData":[OSD([sQuery(id+"F0.wireOp",EDGE,"E0"),sQuery(id+"F0.wireOp",EDGE,"E1.1.0"),sQuery(id+"F0.wireOp",EDGE,"E1.2.0"),sQuery(id+"F0.wireOp",EDGE,"E1.3.0"),sQuery(id+"F0.wireOp",EDGE,"E1.4.0"),sQuery(id+"F0.wireOp",EDGE,"E1.5.0"),sQuery(id+"F0.wireOp",EDGE,"E1.6.0"),sQuery(id+"F0.wireOp",EDGE,"E1.7.0"),sQuery(id+"F0.wireOp",EDGE,"E1.8.0"),sQuery(id+"F0.wireOp",EDGE,"E1.9.0"),sQuery(id+"F0.wireOp",EDGE,"E2.1.10.0"),sQuery(id+"F0.wireOp",EDGE,"E2.1.11.0"),sQuery(id+"F0.wireOp",EDGE,"E3.1.12.0"),sQuery(id+"F0.wireOp",EDGE,"E3.1.13.0")])],"isStart":false});
            chamfer(context, id + "F16", {"entities" : qUnion([Q0]), "width" : 5 * mm, "tangentPropagation" : true});
        }
        {
            var Q0;
            Q0=makeQuery(id+"F15.opExtrude","CAP_FACE",FACE,{"disambiguationData":[OSD([sQuery(id+"F0.wireOp",EDGE,"E0"),sQuery(id+"F0.wireOp",EDGE,"E1.1.0"),sQuery(id+"F0.wireOp",EDGE,"E1.2.0"),sQuery(id+"F0.wireOp",EDGE,"E1.3.0"),sQuery(id+"F0.wireOp",EDGE,"E1.4.0"),sQuery(id+"F0.wireOp",EDGE,"E1.5.0"),sQuery(id+"F0.wireOp",EDGE,"E1.6.0"),sQuery(id+"F0.wireOp",EDGE,"E1.7.0"),sQuery(id+"F0.wireOp",EDGE,"E1.8.0"),sQuery(id+"F0.wireOp",EDGE,"E1.9.0"),sQuery(id+"F0.wireOp",EDGE,"E2.1.10.0"),sQuery(id+"F0.wireOp",EDGE,"E2.1.11.0"),sQuery(id+"F0.wireOp",EDGE,"E3.1.12.0"),sQuery(id+"F0.wireOp",EDGE,"E3.1.13.0")])],"isStart":false});
            extrude(context, id + "F17", {"entities" : qUnion([Q0]), "operationType" : NewBodyOperationType.ADD, "depth" : 25 * mm, "offsetDistance" : 25 * mm});
        }
        {
            var Q0;
            Q0=makeQuery(id+"F17.opExtrude","CAP_FACE",FACE,{"disambiguationData":[OSD([sQuery(id+"F0.wireOp",EDGE,"E0"),sQuery(id+"F0.wireOp",EDGE,"E1.1.0"),sQuery(id+"F0.wireOp",EDGE,"E1.2.0"),sQuery(id+"F0.wireOp",EDGE,"E1.3.0"),sQuery(id+"F0.wireOp",EDGE,"E1.4.0"),sQuery(id+"F0.wireOp",EDGE,"E1.5.0"),sQuery(id+"F0.wireOp",EDGE,"E1.6.0"),sQuery(id+"F0.wireOp",EDGE,"E1.7.0"),sQuery(id+"F0.wireOp",EDGE,"E1.8.0"),sQuery(id+"F0.wireOp",EDGE,"E1.9.0"),sQuery(id+"F0.wireOp",EDGE,"E2.1.10.0"),sQuery(id+"F0.wireOp",EDGE,"E2.1.11.0"),sQuery(id+"F0.wireOp",EDGE,"E3.1.12.0"),sQuery(id+"F0.wireOp",EDGE,"E3.1.13.0")])],"isStart":false});
            chamfer(context, id + "F18", {"entities" : qUnion([Q0]), "width" : 5 * mm, "tangentPropagation" : true});
        }
    });
